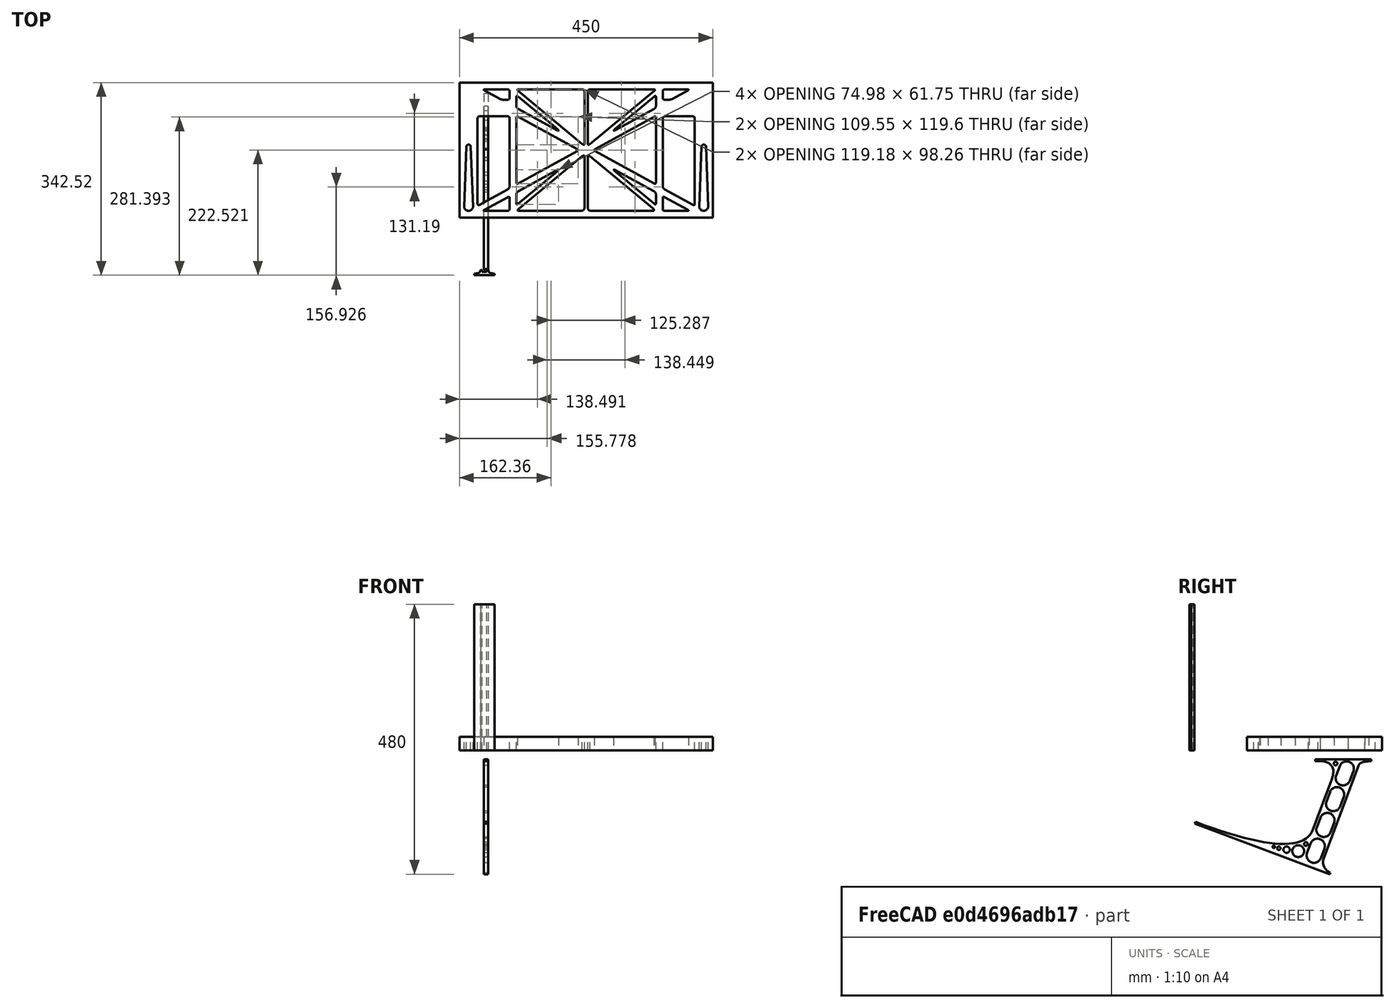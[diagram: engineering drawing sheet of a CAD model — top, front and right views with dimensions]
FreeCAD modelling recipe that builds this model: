
FCSTD DOCUMENT  (FreeCAD 0.19R0.19.2)
Label: laptopStand172FCStd
License: All rights reserved
LicenseURL: http://en.wikipedia.org/wiki/All_rights_reserved
objects: Sketcher::SketchObject×4, Part::Extrusion×3
note: 7 computed .brp shape members not serialized (recipe doc carries the construction recipe); baked Part::Feature solids carry a one-line shape summary decoded from their .brp

FEATURE [Sketcher::SketchObject] Sketch
  FullyConstrained = false
  sketch-geometry (349):
    g0: LineSegment StartX=-10.9272 StartY=-82.7794 StartZ=0 EndX=46.0728 EndY=-51.4823 EndZ=0
    g1: LineSegment StartX=-10.9272 StartY=76.4095 StartZ=0 EndX=-10.9272 EndY=-82.7794 EndZ=0
    g2: LineSegment StartX=46.0728 StartY=76.4095 StartZ=0 EndX=46.0728 EndY=-51.4823 EndZ=0
    g3: LineSegment StartX=-42.9272 StartY=136.221 StartZ=0 EndX=-42.9272 EndY=-103.779 EndZ=0
    g4: LineSegment StartX=407.073 StartY=136.221 StartZ=0 EndX=407.073 EndY=-103.779 EndZ=0
    g5: ArcOfCircle CenterX=-26.9272 CenterY=-83.7794 CenterZ=0 NormalX=0 NormalY=0 NormalZ=1 AngleXU=0 Radius=8 StartAngle=3.14159 EndAngle=6.28319
    g6: ArcOfCircle CenterX=391.073 CenterY=22.1087 CenterZ=0 NormalX=0 NormalY=0 NormalZ=1 AngleXU=0 Radius=8 StartAngle=-4.4e-15 EndAngle=3.14159
    g7: LineSegment StartX=399.073 StartY=22.1087 StartZ=0 EndX=399.073 EndY=-83.7794 EndZ=0
    g8: LineSegment StartX=383.073 StartY=22.1087 StartZ=0 EndX=383.073 EndY=-83.7794 EndZ=0
    g9: ArcOfCircle CenterX=391.073 CenterY=-83.7794 CenterZ=0 NormalX=0 NormalY=0 NormalZ=1 AngleXU=0 Radius=8 StartAngle=3.14159 EndAngle=6.28319
    g10: Circle CenterX=175.022 CenterY=27.0628 CenterZ=0 NormalX=0 NormalY=0 NormalZ=1 AngleXU=0 Radius=1
    g11: Circle CenterX=179.022 CenterY=24.8665 CenterZ=0 NormalX=0 NormalY=0 NormalZ=1 AngleXU=0 Radius=1
    g12: Circle CenterX=179.022 CenterY=27.0628 CenterZ=0 NormalX=0 NormalY=0 NormalZ=1 AngleXU=0 Radius=1
    g13: BSplineCurve PolesCount=3 KnotsCount=2 Degree=2 IsPeriodic=0
    g14: GeomPoint X=175.022 Y=27.0628 Z=0
    g15: GeomPoint X=179.022 Y=27.0628 Z=0
    g16: Circle CenterX=189.124 CenterY=27.0628 CenterZ=0 NormalX=0 NormalY=0 NormalZ=1 AngleXU=0 Radius=1
    g17: Circle CenterX=185.124 CenterY=24.8665 CenterZ=0 NormalX=0 NormalY=0 NormalZ=1 AngleXU=0 Radius=1
    g18: Circle CenterX=185.124 CenterY=27.0628 CenterZ=0 NormalX=0 NormalY=0 NormalZ=1 AngleXU=0 Radius=1
    g19: BSplineCurve PolesCount=3 KnotsCount=2 Degree=2 IsPeriodic=0
    g20: GeomPoint X=189.124 Y=27.0628 Z=0
    g21: GeomPoint X=185.124 Y=27.0628 Z=0
    g22: Circle CenterX=175.022 CenterY=5.37834 CenterZ=0 NormalX=0 NormalY=0 NormalZ=1 AngleXU=0 Radius=1
    g23: Circle CenterX=179.022 CenterY=7.57463 CenterZ=0 NormalX=0 NormalY=0 NormalZ=1 AngleXU=0 Radius=1
    g24: Circle CenterX=179.022 CenterY=5.34704 CenterZ=0 NormalX=0 NormalY=0 NormalZ=1 AngleXU=0 Radius=1
    g25: BSplineCurve PolesCount=3 KnotsCount=2 Degree=2 IsPeriodic=0
    g26: GeomPoint X=175.022 Y=5.37834 Z=0
    g27: GeomPoint X=179.022 Y=5.34704 Z=0
    g28: Circle CenterX=189.124 CenterY=5.37834 CenterZ=0 NormalX=0 NormalY=0 NormalZ=1 AngleXU=0 Radius=1
    g29: Circle CenterX=185.124 CenterY=7.57463 CenterZ=0 NormalX=0 NormalY=0 NormalZ=1 AngleXU=0 Radius=1
    g30: Circle CenterX=185.124 CenterY=5.34704 CenterZ=0 NormalX=0 NormalY=0 NormalZ=1 AngleXU=0 Radius=1
    g31: BSplineCurve PolesCount=3 KnotsCount=2 Degree=2 IsPeriodic=0
    g32: GeomPoint X=189.124 Y=5.37834 Z=0
    g33: GeomPoint X=185.124 Y=5.34704 Z=0
    g34: Circle CenterX=165.871 CenterY=18.1458 CenterZ=0 NormalX=0 NormalY=0 NormalZ=1 AngleXU=0 Radius=1
    g35: Circle CenterX=169.377 CenterY=16.2206 CenterZ=0 NormalX=0 NormalY=0 NormalZ=1 AngleXU=0 Radius=1
    g36: Circle CenterX=165.871 CenterY=14.2954 CenterZ=0 NormalX=0 NormalY=0 NormalZ=1 AngleXU=0 Radius=1
    g37: BSplineCurve PolesCount=3 KnotsCount=2 Degree=2 IsPeriodic=0
    g38: GeomPoint X=165.871 Y=18.1458 Z=0
    g39: GeomPoint X=165.871 Y=14.2954 Z=0
    g40: Circle CenterX=198.275 CenterY=18.1458 CenterZ=0 NormalX=0 NormalY=0 NormalZ=1 AngleXU=0 Radius=1
    g41: Circle CenterX=194.768 CenterY=16.2206 CenterZ=0 NormalX=0 NormalY=0 NormalZ=1 AngleXU=0 Radius=1
    g42: Circle CenterX=198.275 CenterY=14.2954 CenterZ=0 NormalX=0 NormalY=0 NormalZ=1 AngleXU=0 Radius=1
    g43: BSplineCurve PolesCount=3 KnotsCount=2 Degree=2 IsPeriodic=0
    g44: GeomPoint X=198.275 Y=18.1458 Z=0
    g45: GeomPoint X=198.275 Y=14.2954 Z=0
    g46: LineSegment StartX=407.073 StartY=-103.779 StartZ=0 EndX=-42.9272 EndY=-103.779 EndZ=0
    g47: LineSegment StartX=407.073 StartY=136.221 StartZ=0 EndX=-42.9272 EndY=136.221 EndZ=0
    g48: LineSegment StartX=46.0728 StartY=76.4095 StartZ=0 EndX=-10.9272 EndY=76.4095 EndZ=0
    g49: Circle CenterX=125.607 CenterY=54.1951 CenterZ=0 NormalX=0 NormalY=0 NormalZ=1 AngleXU=0 Radius=1
    g50: Circle CenterX=139.632 CenterY=46.4944 CenterZ=0 NormalX=0 NormalY=0 NormalZ=1 AngleXU=0 Radius=1
    g51: Circle CenterX=127.326 CenterY=56.7187 CenterZ=0 NormalX=0 NormalY=0 NormalZ=1 AngleXU=0 Radius=1
    g52: BSplineCurve PolesCount=3 KnotsCount=2 Degree=2 IsPeriodic=0
    g53: GeomPoint X=125.607 Y=54.1951 Z=0
    g54: GeomPoint X=127.326 Y=56.7187 Z=0
    g55: Circle CenterX=236.821 CenterY=56.7187 CenterZ=0 NormalX=0 NormalY=0 NormalZ=1 AngleXU=0 Radius=1
    g56: Circle CenterX=224.513 CenterY=46.4944 CenterZ=0 NormalX=0 NormalY=0 NormalZ=1 AngleXU=0 Radius=1
    g57: Circle CenterX=238.538 CenterY=54.1951 CenterZ=0 NormalX=0 NormalY=0 NormalZ=1 AngleXU=0 Radius=1
    g58: BSplineCurve PolesCount=3 KnotsCount=2 Degree=2 IsPeriodic=0
    g59: GeomPoint X=236.821 Y=56.7187 Z=0
    g60: GeomPoint X=238.538 Y=54.1951 Z=0
    g61: Circle CenterX=238.538 CenterY=-21.7539 CenterZ=0 NormalX=0 NormalY=0 NormalZ=1 AngleXU=0 Radius=1
    g62: Circle CenterX=224.513 CenterY=-14.0532 CenterZ=0 NormalX=0 NormalY=0 NormalZ=1 AngleXU=0 Radius=1
    g63: Circle CenterX=236.821 CenterY=-24.2775 CenterZ=0 NormalX=0 NormalY=0 NormalZ=1 AngleXU=0 Radius=1
    g64: BSplineCurve PolesCount=3 KnotsCount=2 Degree=2 IsPeriodic=0
    g65: GeomPoint X=238.538 Y=-21.7539 Z=0
    g66: GeomPoint X=236.821 Y=-24.2775 Z=0
    g67: Circle CenterX=125.607 CenterY=-21.7539 CenterZ=0 NormalX=0 NormalY=0 NormalZ=1 AngleXU=0 Radius=1
    g68: Circle CenterX=139.632 CenterY=-14.0532 CenterZ=0 NormalX=0 NormalY=0 NormalZ=1 AngleXU=0 Radius=1
    g69: Circle CenterX=127.325 CenterY=-24.2775 CenterZ=0 NormalX=0 NormalY=0 NormalZ=1 AngleXU=0 Radius=1
    g70: BSplineCurve PolesCount=3 KnotsCount=2 Degree=2 IsPeriodic=0
    g71: GeomPoint X=125.607 Y=-21.7539 Z=0
    g72: GeomPoint X=127.325 Y=-24.2775 Z=0
    g73: Circle CenterX=302.996 CenterY=111.695 CenterZ=0 NormalX=0 NormalY=0 NormalZ=1 AngleXU=0 Radius=1
    g74: Circle CenterX=306.073 CenterY=114.251 CenterZ=0 NormalX=0 NormalY=0 NormalZ=1 AngleXU=0 Radius=1
    g75: Circle CenterX=306.073 CenterY=110.251 CenterZ=0 NormalX=0 NormalY=0 NormalZ=1 AngleXU=0 Radius=1
    g76: BSplineCurve PolesCount=3 KnotsCount=2 Degree=2 IsPeriodic=0
    g77: GeomPoint X=302.996 Y=111.695 Z=0
    g78: GeomPoint X=306.073 Y=110.251 Z=0
    g79: Circle CenterX=306.073 CenterY=95.2763 CenterZ=0 NormalX=0 NormalY=0 NormalZ=1 AngleXU=0 Radius=1
    g80: Circle CenterX=306.073 CenterY=91.2763 CenterZ=0 NormalX=0 NormalY=0 NormalZ=1 AngleXU=0 Radius=1
    g81: Circle CenterX=302.567 CenterY=89.3511 CenterZ=0 NormalX=0 NormalY=0 NormalZ=1 AngleXU=0 Radius=1
    g82: BSplineCurve PolesCount=3 KnotsCount=2 Degree=2 IsPeriodic=0
    g83: GeomPoint X=306.073 Y=95.2763 Z=0
    g84: GeomPoint X=302.567 Y=89.3511 Z=0
    g85: LineSegment StartX=306.073 StartY=110.251 StartZ=0 EndX=306.073 EndY=95.2763 EndZ=0
    g86: LineSegment StartX=302.996 StartY=111.695 StartZ=0 EndX=236.821 EndY=56.7187 EndZ=0
    g87: LineSegment StartX=238.538 StartY=54.1951 StartZ=0 EndX=302.567 EndY=89.3511 EndZ=0
    g88: Circle CenterX=61.1496 CenterY=111.695 CenterZ=0 NormalX=0 NormalY=0 NormalZ=1 AngleXU=0 Radius=1
    g89: Circle CenterX=58.0728 CenterY=114.251 CenterZ=0 NormalX=0 NormalY=0 NormalZ=1 AngleXU=0 Radius=1
    g90: Circle CenterX=58.0728 CenterY=110.251 CenterZ=0 NormalX=0 NormalY=0 NormalZ=1 AngleXU=0 Radius=1
    g91: BSplineCurve PolesCount=3 KnotsCount=2 Degree=2 IsPeriodic=0
    g92: GeomPoint X=61.1496 Y=111.695 Z=0
    g93: GeomPoint X=58.0728 Y=110.251 Z=0
    g94: Circle CenterX=61.5791 CenterY=89.3511 CenterZ=0 NormalX=0 NormalY=0 NormalZ=1 AngleXU=0 Radius=1
    g95: Circle CenterX=58.0728 CenterY=91.2763 CenterZ=0 NormalX=0 NormalY=0 NormalZ=1 AngleXU=0 Radius=1
    g96: Circle CenterX=58.0728 CenterY=95.2763 CenterZ=0 NormalX=0 NormalY=0 NormalZ=1 AngleXU=0 Radius=1
    g97: BSplineCurve PolesCount=3 KnotsCount=2 Degree=2 IsPeriodic=0
    g98: GeomPoint X=61.5791 Y=89.3511 Z=0
    g99: GeomPoint X=58.0728 Y=95.2763 Z=0
    g100: LineSegment StartX=58.0728 StartY=110.251 StartZ=0 EndX=58.0728 EndY=95.2763 EndZ=0
    g101: LineSegment StartX=61.1496 StartY=111.695 StartZ=0 EndX=127.326 EndY=56.7187 EndZ=0
    g102: LineSegment StartX=125.607 StartY=54.1951 StartZ=0 EndX=61.5791 EndY=89.3511 EndZ=0
    g103: Circle CenterX=61.5791 CenterY=-56.9099 CenterZ=0 NormalX=0 NormalY=0 NormalZ=1 AngleXU=0 Radius=1
    g104: Circle CenterX=58.0728 CenterY=-58.8351 CenterZ=0 NormalX=0 NormalY=0 NormalZ=1 AngleXU=0 Radius=1
    g105: Circle CenterX=58.0728 CenterY=-62.8351 CenterZ=0 NormalX=0 NormalY=0 NormalZ=1 AngleXU=0 Radius=1
    g106: BSplineCurve PolesCount=3 KnotsCount=2 Degree=2 IsPeriodic=0
    g107: GeomPoint X=61.5791 Y=-56.9099 Z=0
    g108: GeomPoint X=58.0728 Y=-62.8351 Z=0
    g109: Circle CenterX=58.0728 CenterY=-77.8102 CenterZ=0 NormalX=0 NormalY=0 NormalZ=1 AngleXU=0 Radius=1
    g110: Circle CenterX=58.0728 CenterY=-81.8102 CenterZ=0 NormalX=0 NormalY=0 NormalZ=1 AngleXU=0 Radius=1
    g111: Circle CenterX=61.1496 CenterY=-79.2541 CenterZ=0 NormalX=0 NormalY=0 NormalZ=1 AngleXU=0 Radius=1
    g112: BSplineCurve PolesCount=3 KnotsCount=2 Degree=2 IsPeriodic=0
    g113: GeomPoint X=58.0728 Y=-77.8102 Z=0
    g114: GeomPoint X=61.1496 Y=-79.2541 Z=0
    g115: LineSegment StartX=58.0728 StartY=-62.8351 StartZ=0 EndX=58.0728 EndY=-77.8102 EndZ=0
    g116: LineSegment StartX=61.1496 StartY=-79.2541 StartZ=0 EndX=127.325 EndY=-24.2775 EndZ=0
    g117: LineSegment StartX=125.607 StartY=-21.7539 StartZ=0 EndX=61.5791 EndY=-56.9099 EndZ=0
    g118: Circle CenterX=302.567 CenterY=-56.9099 CenterZ=0 NormalX=0 NormalY=0 NormalZ=1 AngleXU=0 Radius=1
    g119: Circle CenterX=306.073 CenterY=-58.8351 CenterZ=0 NormalX=0 NormalY=0 NormalZ=1 AngleXU=0 Radius=1
    g120: Circle CenterX=306.073 CenterY=-62.8351 CenterZ=0 NormalX=0 NormalY=0 NormalZ=1 AngleXU=0 Radius=1
    g121: BSplineCurve PolesCount=3 KnotsCount=2 Degree=2 IsPeriodic=0
    g122: GeomPoint X=302.567 Y=-56.9099 Z=0
    g123: GeomPoint X=306.073 Y=-62.8351 Z=0
    g124: Circle CenterX=302.996 CenterY=-79.2541 CenterZ=0 NormalX=0 NormalY=0 NormalZ=1 AngleXU=0 Radius=1
    g125: Circle CenterX=306.073 CenterY=-81.8102 CenterZ=0 NormalX=0 NormalY=0 NormalZ=1 AngleXU=0 Radius=1
    g126: Circle CenterX=306.073 CenterY=-77.8102 CenterZ=0 NormalX=0 NormalY=0 NormalZ=1 AngleXU=0 Radius=1
    g127: BSplineCurve PolesCount=3 KnotsCount=2 Degree=2 IsPeriodic=0
    g128: GeomPoint X=302.996 Y=-79.2541 Z=0
    g129: GeomPoint X=306.073 Y=-77.8102 Z=0
    g130: LineSegment StartX=306.073 StartY=-62.8351 StartZ=0 EndX=306.073 EndY=-77.8102 EndZ=0
    g131: LineSegment StartX=302.996 StartY=-79.2541 StartZ=0 EndX=236.821 EndY=-24.2775 EndZ=0
    g132: LineSegment StartX=238.538 StartY=-21.7539 StartZ=0 EndX=302.567 EndY=-56.9099 EndZ=0
    g133: Circle CenterX=61.6457 CenterY=-88.8112 CenterZ=0 NormalX=0 NormalY=0 NormalZ=1 AngleXU=0 Radius=1
    g134: Circle CenterX=58.0728 CenterY=-91.7794 CenterZ=0 NormalX=0 NormalY=0 NormalZ=1 AngleXU=0 Radius=1
    g135: Circle CenterX=63.9135 CenterY=-91.7794 CenterZ=0 NormalX=0 NormalY=0 NormalZ=1 AngleXU=0 Radius=1
    g136: BSplineCurve PolesCount=3 KnotsCount=2 Degree=2 IsPeriodic=0
    g137: GeomPoint X=61.6457 Y=-88.8112 Z=0
    g138: GeomPoint X=63.9135 Y=-91.7794 Z=0
    g139: Circle CenterX=179.022 CenterY=-85.8163 CenterZ=0 NormalX=0 NormalY=0 NormalZ=1 AngleXU=0 Radius=1
    g140: Circle CenterX=179.022 CenterY=-91.7794 CenterZ=0 NormalX=0 NormalY=0 NormalZ=1 AngleXU=0 Radius=1
    g141: Circle CenterX=171.895 CenterY=-91.7794 CenterZ=0 NormalX=0 NormalY=0 NormalZ=1 AngleXU=0 Radius=1
    g142: BSplineCurve PolesCount=3 KnotsCount=2 Degree=2 IsPeriodic=0
    g143: GeomPoint X=179.022 Y=-85.8163 Z=0
    g144: GeomPoint X=171.895 Y=-91.7794 Z=0
    g145: Circle CenterX=185.124 CenterY=-86.2028 CenterZ=0 NormalX=0 NormalY=0 NormalZ=1 AngleXU=0 Radius=1
    g146: Circle CenterX=185.124 CenterY=-91.7794 CenterZ=0 NormalX=0 NormalY=0 NormalZ=1 AngleXU=0 Radius=1
    g147: Circle CenterX=191.747 CenterY=-91.7794 CenterZ=0 NormalX=0 NormalY=0 NormalZ=1 AngleXU=0 Radius=1
    g148: BSplineCurve PolesCount=3 KnotsCount=2 Degree=2 IsPeriodic=0
    g149: GeomPoint X=185.124 Y=-86.2028 Z=0
    g150: GeomPoint X=191.747 Y=-91.7794 Z=0
    g151: Circle CenterX=299.888 CenterY=-86.6413 CenterZ=0 NormalX=0 NormalY=0 NormalZ=1 AngleXU=0 Radius=1
    g152: Circle CenterX=306.073 CenterY=-91.7794 CenterZ=0 NormalX=0 NormalY=0 NormalZ=1 AngleXU=0 Radius=1
    g153: Circle CenterX=298.776 CenterY=-91.7794 CenterZ=0 NormalX=0 NormalY=0 NormalZ=1 AngleXU=0 Radius=1
    g154: BSplineCurve PolesCount=3 KnotsCount=2 Degree=2 IsPeriodic=0
    g155: GeomPoint X=299.888 Y=-86.6413 Z=0
    g156: GeomPoint X=298.776 Y=-91.7794 Z=0
    g157: LineSegment StartX=189.124 StartY=5.37834 StartZ=0 EndX=299.888 EndY=-86.6413 EndZ=0
    g158: LineSegment StartX=298.776 StartY=-91.7794 StartZ=0 EndX=191.747 EndY=-91.7794 EndZ=0
    g159: LineSegment StartX=185.124 StartY=-86.2028 StartZ=0 EndX=185.124 EndY=5.34704 EndZ=0
    g160: LineSegment StartX=179.022 StartY=5.34704 StartZ=0 EndX=179.022 EndY=-85.8163 EndZ=0
    g161: LineSegment StartX=171.895 StartY=-91.7794 StartZ=0 EndX=63.9135 EndY=-91.7794 EndZ=0
    g162: LineSegment StartX=61.6457 StartY=-88.8112 StartZ=0 EndX=175.022 EndY=5.37834 EndZ=0
    g163: Circle CenterX=302.073 CenterY=124.221 CenterZ=0 NormalX=0 NormalY=0 NormalZ=1 AngleXU=0 Radius=1
    g164: Circle CenterX=306.073 CenterY=124.221 CenterZ=0 NormalX=0 NormalY=0 NormalZ=1 AngleXU=0 Radius=1
    g165: Circle CenterX=302.996 CenterY=121.665 CenterZ=0 NormalX=0 NormalY=0 NormalZ=1 AngleXU=0 Radius=1
    g166: BSplineCurve PolesCount=3 KnotsCount=2 Degree=2 IsPeriodic=0
    g167: GeomPoint X=302.073 Y=124.221 Z=0
    g168: GeomPoint X=302.996 Y=121.665 Z=0
    g169: Circle CenterX=189.124 CenterY=124.221 CenterZ=0 NormalX=0 NormalY=0 NormalZ=1 AngleXU=0 Radius=1
    g170: Circle CenterX=185.124 CenterY=124.221 CenterZ=0 NormalX=0 NormalY=0 NormalZ=1 AngleXU=0 Radius=1
    g171: Circle CenterX=185.124 CenterY=120.221 CenterZ=0 NormalX=0 NormalY=0 NormalZ=1 AngleXU=0 Radius=1
    g172: BSplineCurve PolesCount=3 KnotsCount=2 Degree=2 IsPeriodic=0
    g173: GeomPoint X=189.124 Y=124.221 Z=0
    g174: GeomPoint X=185.124 Y=120.221 Z=0
    g175: Circle CenterX=175.022 CenterY=124.221 CenterZ=0 NormalX=0 NormalY=0 NormalZ=1 AngleXU=0 Radius=1
    g176: Circle CenterX=179.022 CenterY=124.221 CenterZ=0 NormalX=0 NormalY=0 NormalZ=1 AngleXU=0 Radius=1
    g177: Circle CenterX=179.022 CenterY=120.221 CenterZ=0 NormalX=0 NormalY=0 NormalZ=1 AngleXU=0 Radius=1
    g178: BSplineCurve PolesCount=3 KnotsCount=2 Degree=2 IsPeriodic=0
    g179: GeomPoint X=175.022 Y=124.221 Z=0
    g180: GeomPoint X=179.022 Y=120.221 Z=0
    g181: Circle CenterX=62.0728 CenterY=124.221 CenterZ=0 NormalX=0 NormalY=0 NormalZ=1 AngleXU=0 Radius=1
    g182: Circle CenterX=58.0728 CenterY=124.221 CenterZ=0 NormalX=0 NormalY=0 NormalZ=1 AngleXU=0 Radius=1
    g183: Circle CenterX=61.1496 CenterY=121.665 CenterZ=0 NormalX=0 NormalY=0 NormalZ=1 AngleXU=0 Radius=1
    g184: BSplineCurve PolesCount=3 KnotsCount=2 Degree=2 IsPeriodic=0
    g185: GeomPoint X=62.0728 Y=124.221 Z=0
    g186: GeomPoint X=61.1496 Y=121.665 Z=0
    g187: LineSegment StartX=62.0728 StartY=124.221 StartZ=0 EndX=175.022 EndY=124.221 EndZ=0
    g188: LineSegment StartX=179.022 StartY=120.221 StartZ=0 EndX=179.022 EndY=27.0628 EndZ=0
    g189: LineSegment StartX=185.124 StartY=27.0628 StartZ=0 EndX=185.124 EndY=120.221 EndZ=0
    g190: LineSegment StartX=189.124 StartY=124.221 StartZ=0 EndX=302.073 EndY=124.221 EndZ=0
    g191: LineSegment StartX=302.996 StartY=121.665 StartZ=0 EndX=189.124 EndY=27.0628 EndZ=0
    g192: LineSegment StartX=175.022 StartY=27.0628 StartZ=0 EndX=61.1496 EndY=121.665 EndZ=0
    g193: Circle CenterX=61.5791 CenterY=75.4095 CenterZ=0 NormalX=0 NormalY=0 NormalZ=1 AngleXU=0 Radius=1
    g194: Circle CenterX=58.0728 CenterY=77.3346 CenterZ=0 NormalX=0 NormalY=0 NormalZ=1 AngleXU=0 Radius=1
    g195: Circle CenterX=58.0728 CenterY=73.3346 CenterZ=0 NormalX=0 NormalY=0 NormalZ=1 AngleXU=0 Radius=1
    g196: BSplineCurve PolesCount=3 KnotsCount=2 Degree=2 IsPeriodic=0
    g197: GeomPoint X=61.5791 Y=75.4095 Z=0
    g198: GeomPoint X=58.0728 Y=73.3346 Z=0
    g199: Circle CenterX=58.0728 CenterY=-40.8935 CenterZ=0 NormalX=0 NormalY=0 NormalZ=1 AngleXU=0 Radius=1
    g200: Circle CenterX=58.0728 CenterY=-44.8935 CenterZ=0 NormalX=0 NormalY=0 NormalZ=1 AngleXU=0 Radius=1
    g201: Circle CenterX=61.5791 CenterY=-42.9683 CenterZ=0 NormalX=0 NormalY=0 NormalZ=1 AngleXU=0 Radius=1
    g202: BSplineCurve PolesCount=3 KnotsCount=2 Degree=2 IsPeriodic=0
    g203: GeomPoint X=58.0728 Y=-40.8935 Z=0
    g204: GeomPoint X=61.5791 Y=-42.9683 Z=0
    g205: LineSegment StartX=61.5791 StartY=-42.9683 StartZ=0 EndX=165.871 EndY=14.2954 EndZ=0
    g206: LineSegment StartX=165.871 StartY=18.1458 StartZ=0 EndX=61.5791 EndY=75.4095 EndZ=0
    g207: LineSegment StartX=58.0728 StartY=73.3346 StartZ=0 EndX=58.0728 EndY=-40.8935 EndZ=0
    g208: Circle CenterX=302.567 CenterY=-42.9683 CenterZ=0 NormalX=0 NormalY=0 NormalZ=1 AngleXU=0 Radius=1
    g209: Circle CenterX=306.073 CenterY=-44.8935 CenterZ=0 NormalX=0 NormalY=0 NormalZ=1 AngleXU=0 Radius=1
    g210: Circle CenterX=306.073 CenterY=-40.8935 CenterZ=0 NormalX=0 NormalY=0 NormalZ=1 AngleXU=0 Radius=1
    g211: BSplineCurve PolesCount=3 KnotsCount=2 Degree=2 IsPeriodic=0
    g212: GeomPoint X=302.567 Y=-42.9683 Z=0
    g213: GeomPoint X=306.073 Y=-40.8935 Z=0
    g214: Circle CenterX=306.073 CenterY=73.3346 CenterZ=0 NormalX=0 NormalY=0 NormalZ=1 AngleXU=0 Radius=1
    g215: Circle CenterX=306.073 CenterY=77.3346 CenterZ=0 NormalX=0 NormalY=0 NormalZ=1 AngleXU=0 Radius=1
    g216: Circle CenterX=302.567 CenterY=75.4095 CenterZ=0 NormalX=0 NormalY=0 NormalZ=1 AngleXU=0 Radius=1
    g217: BSplineCurve PolesCount=3 KnotsCount=2 Degree=2 IsPeriodic=0
    g218: GeomPoint X=306.073 Y=73.3346 Z=0
    g219: GeomPoint X=302.567 Y=75.4095 Z=0
    g220: LineSegment StartX=302.567 StartY=-42.9683 StartZ=0 EndX=198.275 EndY=14.2954 EndZ=0
    g221: LineSegment StartX=198.275 StartY=18.1458 StartZ=0 EndX=302.567 EndY=75.4095 EndZ=0
    g222: LineSegment StartX=306.073 StartY=73.3346 StartZ=0 EndX=306.073 EndY=-40.8935 EndZ=0
    g223: LineSegment StartX=322.073 StartY=105.865 StartZ=0 EndX=328.643 EndY=105.865 EndZ=0
    g224: LineSegment StartX=318.073 StartY=120.221 StartZ=0 EndX=318.073 EndY=109.865 EndZ=0
    g225: LineSegment StartX=336.157 StartY=107.779 StartZ=0 EndX=362.567 EndY=122.294 EndZ=0
    g226: Circle CenterX=362.073 CenterY=124.221 CenterZ=0 NormalX=0 NormalY=0 NormalZ=1 AngleXU=0 Radius=1
    g227: Circle CenterX=366.073 CenterY=124.221 CenterZ=0 NormalX=0 NormalY=0 NormalZ=1 AngleXU=0 Radius=1
    g228: Circle CenterX=362.567 CenterY=122.294 CenterZ=0 NormalX=0 NormalY=0 NormalZ=1 AngleXU=0 Radius=1
    g229: BSplineCurve PolesCount=3 KnotsCount=2 Degree=2 IsPeriodic=0
    g230: GeomPoint X=362.073 Y=124.221 Z=0
    g231: GeomPoint X=362.567 Y=122.294 Z=0
    g232: Circle CenterX=322.073 CenterY=124.221 CenterZ=0 NormalX=0 NormalY=0 NormalZ=1 AngleXU=0 Radius=1
    g233: Circle CenterX=318.073 CenterY=124.221 CenterZ=0 NormalX=0 NormalY=0 NormalZ=1 AngleXU=0 Radius=1
    g234: Circle CenterX=318.073 CenterY=120.221 CenterZ=0 NormalX=0 NormalY=0 NormalZ=1 AngleXU=0 Radius=1
    g235: BSplineCurve PolesCount=3 KnotsCount=2 Degree=2 IsPeriodic=0
    g236: GeomPoint X=322.073 Y=124.221 Z=0
    g237: GeomPoint X=318.073 Y=120.221 Z=0
    g238: Circle CenterX=322.073 CenterY=105.865 CenterZ=0 NormalX=0 NormalY=0 NormalZ=1 AngleXU=0 Radius=1
    g239: Circle CenterX=318.073 CenterY=105.865 CenterZ=0 NormalX=0 NormalY=0 NormalZ=1 AngleXU=0 Radius=1
    g240: Circle CenterX=318.073 CenterY=109.865 CenterZ=0 NormalX=0 NormalY=0 NormalZ=1 AngleXU=0 Radius=1
    g241: BSplineCurve PolesCount=3 KnotsCount=2 Degree=2 IsPeriodic=0
    g242: GeomPoint X=322.073 Y=105.865 Z=0
    g243: GeomPoint X=318.073 Y=109.865 Z=0
    g244: Circle CenterX=336.157 CenterY=107.779 CenterZ=0 NormalX=0 NormalY=0 NormalZ=1 AngleXU=0 Radius=1
    g245: Circle CenterX=332.651 CenterY=105.853 CenterZ=0 NormalX=0 NormalY=0 NormalZ=1 AngleXU=0 Radius=1
    g246: Circle CenterX=328.643 CenterY=105.865 CenterZ=0 NormalX=0 NormalY=0 NormalZ=1 AngleXU=0 Radius=1
    g247: BSplineCurve PolesCount=3 KnotsCount=2 Degree=2 IsPeriodic=0
    g248: GeomPoint X=336.157 Y=107.779 Z=0
    g249: GeomPoint X=328.643 Y=105.865 Z=0
    g250: LineSegment StartX=322.073 StartY=124.221 StartZ=0 EndX=362.073 EndY=124.221 EndZ=0
    g251: Circle CenterX=371.567 CenterY=-80.8644 CenterZ=0 NormalX=0 NormalY=0 NormalZ=1 AngleXU=0 Radius=1
    g252: Circle CenterX=375.073 CenterY=-82.7896 CenterZ=0 NormalX=0 NormalY=0 NormalZ=1 AngleXU=0 Radius=1
    g253: Circle CenterX=375.073 CenterY=-78.7896 CenterZ=0 NormalX=0 NormalY=0 NormalZ=1 AngleXU=0 Radius=1
    g254: BSplineCurve PolesCount=3 KnotsCount=2 Degree=2 IsPeriodic=0
    g255: GeomPoint X=371.567 Y=-80.8644 Z=0
    g256: GeomPoint X=375.073 Y=-78.7896 Z=0
    g257: Circle CenterX=321.579 CenterY=-53.4075 CenterZ=0 NormalX=0 NormalY=0 NormalZ=1 AngleXU=0 Radius=1
    g258: Circle CenterX=318.073 CenterY=-51.4823 CenterZ=0 NormalX=0 NormalY=0 NormalZ=1 AngleXU=0 Radius=1
    g259: Circle CenterX=318.073 CenterY=-47.4805 CenterZ=0 NormalX=0 NormalY=0 NormalZ=1 AngleXU=0 Radius=1
    g260: BSplineCurve PolesCount=3 KnotsCount=2 Degree=2 IsPeriodic=0
    g261: GeomPoint X=321.579 Y=-53.4075 Z=0
    g262: GeomPoint X=318.073 Y=-47.4805 Z=0
    g263: LineSegment StartX=371.567 StartY=-80.8644 StartZ=0 EndX=321.579 EndY=-53.4075 EndZ=0
    g264: Circle CenterX=321.579 CenterY=-67.3492 CenterZ=0 NormalX=0 NormalY=0 NormalZ=1 AngleXU=0 Radius=1
    g265: Circle CenterX=318.073 CenterY=-65.424 CenterZ=0 NormalX=0 NormalY=0 NormalZ=1 AngleXU=0 Radius=1
    g266: Circle CenterX=318.073 CenterY=-69.424 CenterZ=0 NormalX=0 NormalY=0 NormalZ=1 AngleXU=0 Radius=1
    g267: BSplineCurve PolesCount=3 KnotsCount=2 Degree=2 IsPeriodic=0
    g268: GeomPoint X=321.579 Y=-67.3492 Z=0
    g269: GeomPoint X=318.073 Y=-69.424 Z=0
    g270: Circle CenterX=362.567 CenterY=-89.8542 CenterZ=0 NormalX=0 NormalY=0 NormalZ=1 AngleXU=0 Radius=1
    g271: Circle CenterX=366.073 CenterY=-91.7794 CenterZ=0 NormalX=0 NormalY=0 NormalZ=1 AngleXU=0 Radius=1
    g272: Circle CenterX=362.073 CenterY=-91.7794 CenterZ=0 NormalX=0 NormalY=0 NormalZ=1 AngleXU=0 Radius=1
    g273: BSplineCurve PolesCount=3 KnotsCount=2 Degree=2 IsPeriodic=0
    g274: GeomPoint X=362.567 Y=-89.8542 Z=0
    g275: GeomPoint X=362.073 Y=-91.7794 Z=0
    g276: Circle CenterX=322.073 CenterY=-91.7794 CenterZ=0 NormalX=0 NormalY=0 NormalZ=1 AngleXU=0 Radius=1
    g277: Circle CenterX=318.073 CenterY=-91.7794 CenterZ=0 NormalX=0 NormalY=0 NormalZ=1 AngleXU=0 Radius=1
    g278: Circle CenterX=318.073 CenterY=-87.7794 CenterZ=0 NormalX=0 NormalY=0 NormalZ=1 AngleXU=0 Radius=1
    g279: BSplineCurve PolesCount=3 KnotsCount=2 Degree=2 IsPeriodic=0
    g280: GeomPoint X=322.073 Y=-91.7794 Z=0
    g281: GeomPoint X=318.073 Y=-87.7794 Z=0
    g282: LineSegment StartX=362.567 StartY=-89.8542 StartZ=0 EndX=321.579 EndY=-67.3492 EndZ=0
    g283: LineSegment StartX=318.073 StartY=-69.424 StartZ=0 EndX=318.073 EndY=-87.7794 EndZ=0
    g284: LineSegment StartX=322.073 StartY=-91.7794 StartZ=0 EndX=362.073 EndY=-91.7794 EndZ=0
    g285: Circle CenterX=2.07281 CenterY=124.221 CenterZ=0 NormalX=0 NormalY=0 NormalZ=1 AngleXU=0 Radius=1
    g286: Circle CenterX=1.57905 CenterY=122.295 CenterZ=0 NormalX=0 NormalY=0 NormalZ=1 AngleXU=0 Radius=1
    g287: BSplineCurve PolesCount=3 KnotsCount=2 Degree=2 IsPeriodic=0
    g288: GeomPoint X=2.07281 Y=124.221 Z=0
    g289: GeomPoint X=1.57905 Y=122.295 Z=0
    g290: Circle CenterX=42.0728 CenterY=124.221 CenterZ=0 NormalX=0 NormalY=0 NormalZ=1 AngleXU=0 Radius=1
    g291: Circle CenterX=46.0728 CenterY=124.221 CenterZ=0 NormalX=0 NormalY=0 NormalZ=1 AngleXU=0 Radius=1
    g292: Circle CenterX=46.0728 CenterY=120.221 CenterZ=0 NormalX=0 NormalY=0 NormalZ=1 AngleXU=0 Radius=1
    g293: BSplineCurve PolesCount=3 KnotsCount=2 Degree=2 IsPeriodic=0
    g294: GeomPoint X=42.0728 Y=124.221 Z=0
    g295: GeomPoint X=46.0728 Y=120.221 Z=0
    g296: Circle CenterX=46.0728 CenterY=109.865 CenterZ=0 NormalX=0 NormalY=0 NormalZ=1 AngleXU=0 Radius=1
    g297: Circle CenterX=46.0728 CenterY=105.865 CenterZ=0 NormalX=0 NormalY=0 NormalZ=1 AngleXU=0 Radius=1
    g298: Circle CenterX=42.0728 CenterY=105.865 CenterZ=0 NormalX=0 NormalY=0 NormalZ=1 AngleXU=0 Radius=1
    g299: BSplineCurve PolesCount=3 KnotsCount=2 Degree=2 IsPeriodic=0
    g300: GeomPoint X=46.0728 Y=109.865 Z=0
    g301: GeomPoint X=42.0728 Y=105.865 Z=0
    g302: Circle CenterX=35.5028 CenterY=105.865 CenterZ=0 NormalX=0 NormalY=0 NormalZ=1 AngleXU=0 Radius=1
    g303: Circle CenterX=31.5028 CenterY=105.865 CenterZ=0 NormalX=0 NormalY=0 NormalZ=1 AngleXU=0 Radius=1
    g304: Circle CenterX=27.9965 CenterY=107.79 CenterZ=0 NormalX=0 NormalY=0 NormalZ=1 AngleXU=0 Radius=1
    g305: BSplineCurve PolesCount=3 KnotsCount=2 Degree=2 IsPeriodic=0
    g306: GeomPoint X=35.5028 Y=105.865 Z=0
    g307: GeomPoint X=27.9965 Y=107.79 Z=0
    g308: LineSegment StartX=2.07281 StartY=124.221 StartZ=0 EndX=42.0728 EndY=124.221 EndZ=0
    g309: LineSegment StartX=46.0728 StartY=120.221 StartZ=0 EndX=46.0728 EndY=109.865 EndZ=0
    g310: LineSegment StartX=42.0728 StartY=105.865 StartZ=0 EndX=35.5028 EndY=105.865 EndZ=0
    g311: LineSegment StartX=27.9965 StartY=107.79 StartZ=0 EndX=1.57905 EndY=122.295 EndZ=0
    g312: Circle CenterX=42.5666 CenterY=-67.3492 CenterZ=0 NormalX=0 NormalY=0 NormalZ=1 AngleXU=0 Radius=1
    g313: Circle CenterX=46.0728 CenterY=-65.424 CenterZ=0 NormalX=0 NormalY=0 NormalZ=1 AngleXU=0 Radius=1
    g314: Circle CenterX=46.0728 CenterY=-69.424 CenterZ=0 NormalX=0 NormalY=0 NormalZ=1 AngleXU=0 Radius=1
    g315: BSplineCurve PolesCount=3 KnotsCount=2 Degree=2 IsPeriodic=0
    g316: GeomPoint X=42.5666 Y=-67.3492 Z=0
    g317: GeomPoint X=46.0728 Y=-69.424 Z=0
    g318: Circle CenterX=46.0728 CenterY=-87.7794 CenterZ=0 NormalX=0 NormalY=0 NormalZ=1 AngleXU=0 Radius=1
    g319: Circle CenterX=46.0728 CenterY=-91.7794 CenterZ=0 NormalX=0 NormalY=0 NormalZ=1 AngleXU=0 Radius=1
    g320: Circle CenterX=42.0728 CenterY=-91.7794 CenterZ=0 NormalX=0 NormalY=0 NormalZ=1 AngleXU=0 Radius=1
    g321: BSplineCurve PolesCount=3 KnotsCount=2 Degree=2 IsPeriodic=0
    g322: GeomPoint X=46.0728 Y=-87.7794 Z=0
    g323: GeomPoint X=42.0728 Y=-91.7794 Z=0
    g324: Circle CenterX=2.07281 CenterY=-91.7794 CenterZ=0 NormalX=0 NormalY=0 NormalZ=1 AngleXU=0 Radius=1
    g325: Circle CenterX=-1.92719 CenterY=-91.7794 CenterZ=0 NormalX=0 NormalY=0 NormalZ=1 AngleXU=0 Radius=1
    g326: Circle CenterX=1.57905 CenterY=-89.8542 CenterZ=0 NormalX=0 NormalY=0 NormalZ=1 AngleXU=0 Radius=1
    g327: BSplineCurve PolesCount=3 KnotsCount=2 Degree=2 IsPeriodic=0
    g328: GeomPoint X=2.07281 Y=-91.7794 Z=0
    g329: GeomPoint X=1.57905 Y=-89.8542 Z=0
    g330: LineSegment StartX=2.07281 StartY=-91.7794 StartZ=0 EndX=42.0728 EndY=-91.7794 EndZ=0
    g331: LineSegment StartX=46.0728 StartY=-87.7794 StartZ=0 EndX=46.0728 EndY=-69.424 EndZ=0
    g332: LineSegment StartX=42.5666 StartY=-67.3492 StartZ=0 EndX=1.57905 EndY=-89.8542 EndZ=0
    g333: Circle CenterX=322.073 CenterY=76.4095 CenterZ=0 NormalX=0 NormalY=0 NormalZ=1 AngleXU=0 Radius=4
    g334: BSplineCurve PolesCount=3 KnotsCount=2 Degree=2 IsPeriodic=0
    g335: GeomPoint X=318.073 Y=72.4095 Z=0
    g336: GeomPoint X=322.073 Y=76.4095 Z=0
    g337: Circle CenterX=375.073 CenterY=72.4095 CenterZ=0 NormalX=0 NormalY=0 NormalZ=1 AngleXU=0 Radius=1
    g338: Circle CenterX=375.073 CenterY=76.4095 CenterZ=0 NormalX=0 NormalY=0 NormalZ=1 AngleXU=0 Radius=1
    g339: Circle CenterX=371.073 CenterY=76.4095 CenterZ=0 NormalX=0 NormalY=0 NormalZ=1 AngleXU=0 Radius=1
    g340: BSplineCurve PolesCount=3 KnotsCount=2 Degree=2 IsPeriodic=0
    g341: GeomPoint X=375.073 Y=72.4095 Z=0
    g342: GeomPoint X=371.073 Y=76.4095 Z=0
    g343: LineSegment StartX=322.073 StartY=76.4095 StartZ=0 EndX=371.073 EndY=76.4095 EndZ=0
    g344: LineSegment StartX=318.073 StartY=72.4095 StartZ=0 EndX=318.073 EndY=-47.4805 EndZ=0
    g345: LineSegment StartX=375.073 StartY=72.4095 StartZ=0 EndX=375.073 EndY=-78.7896 EndZ=0
    g346: ArcOfCircle CenterX=-26.9272 CenterY=22.1087 CenterZ=0 NormalX=0 NormalY=0 NormalZ=1 AngleXU=0 Radius=4 StartAngle=5e-16 EndAngle=3.14159
    g347: LineSegment StartX=-30.9272 StartY=22.1087 StartZ=0 EndX=-34.9272 EndY=-83.7794 EndZ=0
    g348: LineSegment StartX=-18.9272 StartY=-83.7794 StartZ=0 EndX=-22.9272 EndY=22.1087 EndZ=0
  constraints (572):
    c: Coincident(g0,g2)
    c: Block(g0)
    c: Block(g1)
    c: Vertical(g3)
    c: Vertical(g4)
    c: Block(g4)
    c: Block(g3)
    c: Tangent(g6,g7) = 1.5708
    c: Tangent(g7,g9) = 1.5708
    c: Equal(g6,g9)
    c: Coincident(g8,g6)
    c: Coincident(g8,g9)
    c: Block(g7)
    c: Block(g8)
    c: Weight(g10) = 1
    c: Equal(g10,g11)
    c: Equal(g10,g12)
    c: InternalAlignment(g10,g13)
    c: InternalAlignment(g11,g13)
    c: InternalAlignment(g12,g13)
    c: InternalAlignment(g14,g13)
    c: InternalAlignment(g15,g13)
    c: Weight(g16) = 1
    c: Equal(g16,g17)
    c: Equal(g16,g18)
    c: InternalAlignment(g16,g19)
    c: InternalAlignment(g17,g19)
    c: InternalAlignment(g18,g19)
    c: InternalAlignment(g20,g19)
    c: InternalAlignment(g21,g19)
    c: Block(g19)
    c: Block(g13)
    c: Weight(g22) = 1
    c: Equal(g22,g23)
    c: Equal(g22,g24)
    c: InternalAlignment(g22,g25)
    c: InternalAlignment(g23,g25)
    c: InternalAlignment(g24,g25)
    c: InternalAlignment(g26,g25)
    c: InternalAlignment(g27,g25)
    c: Weight(g28) = 1
    c: Equal(g28,g29)
    c: Equal(g28,g30)
    c: InternalAlignment(g28,g31)
    c: InternalAlignment(g29,g31)
    c: InternalAlignment(g30,g31)
    c: InternalAlignment(g32,g31)
    c: InternalAlignment(g33,g31)
    c: Block(g31)
    c: Block(g25)
    c: Weight(g34) = 1
    c: Equal(g34,g35)
    c: Equal(g34,g36)
    c: InternalAlignment(g34,g37)
    c: InternalAlignment(g35,g37)
    c: InternalAlignment(g36,g37)
    c: InternalAlignment(g38,g37)
    c: InternalAlignment(g39,g37)
    c: Weight(g40) = 1
    c: Equal(g40,g41)
    c: Equal(g40,g42)
    c: InternalAlignment(g40,g43)
    c: InternalAlignment(g41,g43)
    c: InternalAlignment(g42,g43)
    c: InternalAlignment(g44,g43)
    c: InternalAlignment(g45,g43)
    c: Block(g37)
    c: Block(g43)
    c: Coincident(g46,g4)
    c: Coincident(g46,g3)
    c: Horizontal(g46)
    c: Distance(g46) = 450
    c: Coincident(g47,g4)
    c: Coincident(g47,g3)
    c: Horizontal(g47)
    c: Horizontal(g48)
    c: Coincident(g2,g48)
    c: Block(g48)
    c: Coincident(g1,g48)
    c: Weight(g49) = 1
    c: Equal(g49,g50)
    c: Equal(g49,g51)
    c: InternalAlignment(g49,g52)
    c: InternalAlignment(g50,g52)
    c: InternalAlignment(g51,g52)
    c: InternalAlignment(g53,g52)
    c: InternalAlignment(g54,g52)
    c: Block(g52)
    c: Weight(g55) = 1
    c: Equal(g55,g56)
    c: Equal(g55,g57)
    c: InternalAlignment(g55,g58)
    c: InternalAlignment(g56,g58)
    c: InternalAlignment(g57,g58)
    c: InternalAlignment(g59,g58)
    c: InternalAlignment(g60,g58)
    c: Block(g58)
    c: Weight(g61) = 1
    c: Equal(g61,g62)
    c: Equal(g61,g63)
    c: InternalAlignment(g61,g64)
    c: InternalAlignment(g62,g64)
    c: InternalAlignment(g63,g64)
    c: InternalAlignment(g65,g64)
    c: InternalAlignment(g66,g64)
    c: Block(g64)
    c: Weight(g67) = 1
    c: Equal(g67,g68)
    c: Equal(g67,g69)
    c: InternalAlignment(g67,g70)
    c: InternalAlignment(g68,g70)
    c: InternalAlignment(g69,g70)
    c: InternalAlignment(g71,g70)
    c: InternalAlignment(g72,g70)
    c: Block(g70)
    c: Weight(g73) = 1
    c: Equal(g73,g74)
    c: Equal(g73,g75)
    c: InternalAlignment(g73,g76)
    c: InternalAlignment(g74,g76)
    c: InternalAlignment(g75,g76)
    c: InternalAlignment(g77,g76)
    c: InternalAlignment(g78,g76)
    c: Weight(g79) = 1
    c: Equal(g79,g80)
    c: Equal(g79,g81)
    c: InternalAlignment(g79,g82)
    c: InternalAlignment(g80,g82)
    c: InternalAlignment(g81,g82)
    c: InternalAlignment(g83,g82)
    c: InternalAlignment(g84,g82)
    c: Block(g76)
    c: Block(g82)
    c: Coincident(g85,g76)
    c: Coincident(g85,g82)
    c: Vertical(g85)
    c: Coincident(g86,g76)
    c: Coincident(g86,g58)
    c: Coincident(g87,g58)
    c: Coincident(g87,g82)
    c: Weight(g88) = 1
    c: Equal(g88,g89)
    c: Equal(g88,g90)
    c: InternalAlignment(g88,g91)
    c: InternalAlignment(g89,g91)
    c: InternalAlignment(g90,g91)
    c: InternalAlignment(g92,g91)
    c: InternalAlignment(g93,g91)
    c: Weight(g94) = 1
    c: Equal(g94,g95)
    c: Equal(g94,g96)
    c: InternalAlignment(g94,g97)
    c: InternalAlignment(g95,g97)
    c: InternalAlignment(g96,g97)
    c: InternalAlignment(g98,g97)
    c: InternalAlignment(g99,g97)
    c: Block(g91)
    c: Block(g97)
    c: Coincident(g100,g91)
    c: Coincident(g100,g97)
    c: Vertical(g100)
    c: Coincident(g101,g91)
    c: Coincident(g101,g52)
    c: Coincident(g102,g52)
    c: Coincident(g102,g97)
    c: Weight(g103) = 1
    c: Equal(g103,g104)
    c: Equal(g103,g105)
    c: InternalAlignment(g103,g106)
    c: InternalAlignment(g104,g106)
    c: InternalAlignment(g105,g106)
    c: InternalAlignment(g107,g106)
    c: InternalAlignment(g108,g106)
    c: Weight(g109) = 1
    c: Equal(g109,g110)
    c: Equal(g109,g111)
    c: InternalAlignment(g109,g112)
    c: InternalAlignment(g110,g112)
    c: InternalAlignment(g111,g112)
    c: InternalAlignment(g113,g112)
    c: InternalAlignment(g114,g112)
    c: Block(g106)
    c: Block(g112)
    c: Coincident(g115,g106)
    c: Coincident(g115,g112)
    c: Vertical(g115)
    c: Coincident(g116,g112)
    c: Coincident(g116,g70)
    c: Coincident(g117,g70)
    c: Coincident(g117,g106)
    c: Weight(g118) = 1
    c: Equal(g118,g119)
    c: Equal(g118,g120)
    c: InternalAlignment(g118,g121)
    c: InternalAlignment(g119,g121)
    c: InternalAlignment(g120,g121)
    c: InternalAlignment(g122,g121)
    c: InternalAlignment(g123,g121)
    c: Weight(g124) = 1
    c: Equal(g124,g125)
    c: Equal(g124,g126)
    c: InternalAlignment(g124,g127)
    c: InternalAlignment(g125,g127)
    c: InternalAlignment(g126,g127)
    c: InternalAlignment(g128,g127)
    c: InternalAlignment(g129,g127)
    c: Block(g121)
    c: Block(g127)
    c: Coincident(g130,g121)
    c: Coincident(g130,g127)
    c: Vertical(g130)
    c: Coincident(g131,g127)
    c: Coincident(g131,g64)
    c: Coincident(g132,g64)
    c: Coincident(g132,g121)
    c: Weight(g133) = 1
    c: Equal(g133,g134)
    c: Equal(g133,g135)
    c: InternalAlignment(g133,g136)
    c: InternalAlignment(g134,g136)
    c: InternalAlignment(g135,g136)
    c: InternalAlignment(g137,g136)
    c: InternalAlignment(g138,g136)
    c: Weight(g139) = 1
    c: Equal(g139,g140)
    c: Equal(g139,g141)
    c: InternalAlignment(g139,g142)
    c: InternalAlignment(g140,g142)
    c: InternalAlignment(g141,g142)
    c: InternalAlignment(g143,g142)
    c: InternalAlignment(g144,g142)
    c: Weight(g145) = 1
    c: Equal(g145,g146)
    c: Equal(g145,g147)
    c: InternalAlignment(g145,g148)
    c: InternalAlignment(g146,g148)
    c: InternalAlignment(g147,g148)
    c: InternalAlignment(g149,g148)
    c: InternalAlignment(g150,g148)
    c: Weight(g151) = 1
    c: Equal(g151,g152)
    c: Equal(g151,g153)
    c: InternalAlignment(g151,g154)
    c: InternalAlignment(g152,g154)
    c: InternalAlignment(g153,g154)
    c: InternalAlignment(g155,g154)
    c: InternalAlignment(g156,g154)
    c: Block(g154)
    c: Block(g148)
    c: Block(g142)
    c: Block(g136)
    c: Coincident(g157,g31)
    c: Coincident(g157,g154)
    c: Coincident(g158,g154)
    c: Coincident(g158,g148)
    c: Horizontal(g158)
    c: Coincident(g159,g148)
    c: Coincident(g159,g31)
    c: Vertical(g159)
    c: Coincident(g160,g25)
    c: Coincident(g160,g142)
    c: Vertical(g160)
    c: Coincident(g161,g142)
    c: Coincident(g161,g136)
    c: Horizontal(g161)
    c: Coincident(g162,g136)
    c: Coincident(g162,g25)
    c: Weight(g163) = 1
    c: Equal(g163,g164)
    c: Equal(g163,g165)
    c: InternalAlignment(g163,g166)
    c: InternalAlignment(g164,g166)
    c: InternalAlignment(g165,g166)
    c: InternalAlignment(g167,g166)
    c: InternalAlignment(g168,g166)
    c: Weight(g169) = 1
    c: Equal(g169,g170)
    c: Equal(g169,g171)
    c: InternalAlignment(g169,g172)
    c: InternalAlignment(g170,g172)
    c: InternalAlignment(g171,g172)
    c: InternalAlignment(g173,g172)
    c: InternalAlignment(g174,g172)
    c: Weight(g175) = 1
    c: Equal(g175,g176)
    c: Equal(g175,g177)
    c: InternalAlignment(g175,g178)
    c: InternalAlignment(g176,g178)
    c: InternalAlignment(g177,g178)
    c: InternalAlignment(g179,g178)
    c: InternalAlignment(g180,g178)
    c: Weight(g181) = 1
    c: Equal(g181,g182)
    c: Equal(g181,g183)
    c: InternalAlignment(g181,g184)
    c: InternalAlignment(g182,g184)
    c: InternalAlignment(g183,g184)
    c: InternalAlignment(g185,g184)
    c: InternalAlignment(g186,g184)
    c: Block(g184)
    c: Block(g178)
    c: Block(g172)
    c: Block(g166)
    c: Coincident(g187,g184)
    c: Coincident(g187,g178)
    c: Horizontal(g187)
    c: Coincident(g188,g178)
    c: Coincident(g188,g13)
    c: Vertical(g188)
    c: Coincident(g189,g19)
    c: Coincident(g189,g172)
    c: Vertical(g189)
    c: Coincident(g190,g172)
    c: Coincident(g190,g166)
    c: Horizontal(g190)
    c: Coincident(g191,g166)
    c: Coincident(g191,g19)
    c: Coincident(g192,g13)
    c: Weight(g193) = 1
    c: Equal(g193,g194)
    c: Equal(g193,g195)
    c: InternalAlignment(g193,g196)
    c: InternalAlignment(g194,g196)
    c: InternalAlignment(g195,g196)
    c: InternalAlignment(g197,g196)
    c: InternalAlignment(g198,g196)
    c: Weight(g199) = 1
    c: Equal(g199,g200)
    c: Equal(g199,g201)
    c: InternalAlignment(g199,g202)
    c: InternalAlignment(g200,g202)
    c: InternalAlignment(g201,g202)
    c: InternalAlignment(g203,g202)
    c: InternalAlignment(g204,g202)
    c: Block(g202)
    c: Block(g196)
    c: Coincident(g205,g202)
    c: Coincident(g205,g37)
    c: Coincident(g206,g37)
    c: Coincident(g206,g196)
    c: Coincident(g207,g196)
    c: Coincident(g207,g202)
    c: Vertical(g207)
    c: Weight(g208) = 1
    c: Equal(g208,g209)
    c: Equal(g208,g210)
    c: InternalAlignment(g208,g211)
    c: InternalAlignment(g209,g211)
    c: InternalAlignment(g210,g211)
    c: InternalAlignment(g212,g211)
    c: InternalAlignment(g213,g211)
    c: Weight(g214) = 1
    c: Equal(g214,g215)
    c: Equal(g214,g216)
    c: InternalAlignment(g214,g217)
    c: InternalAlignment(g215,g217)
    c: InternalAlignment(g216,g217)
    c: InternalAlignment(g218,g217)
    c: InternalAlignment(g219,g217)
    c: Block(g217)
    c: Block(g211)
    c: Coincident(g220,g211)
    c: Coincident(g220,g43)
    c: Coincident(g221,g43)
    c: Coincident(g221,g217)
    c: Coincident(g222,g217)
    c: Coincident(g222,g211)
    c: Vertical(g222)
    c: Horizontal(g223)
    c: Block(g223)
    c: Vertical(g224)
    c: Block(g224)
    c: Block(g225)
    c: Weight(g226) = 1
    c: Equal(g226,g227)
    c: Equal(g226,g228)
    c: InternalAlignment(g226,g229)
    c: InternalAlignment(g227,g229)
    c: InternalAlignment(g228,g229)
    c: InternalAlignment(g230,g229)
    c: InternalAlignment(g231,g229)
    c: Weight(g232) = 1
    c: Equal(g232,g233)
    c: Equal(g232,g234)
    c: InternalAlignment(g232,g235)
    c: InternalAlignment(g233,g235)
    c: InternalAlignment(g234,g235)
    c: InternalAlignment(g236,g235)
    c: InternalAlignment(g237,g235)
    c: Weight(g238) = 1
    c: Equal(g238,g239)
    c: Equal(g238,g240)
    c: InternalAlignment(g238,g241)
    c: InternalAlignment(g239,g241)
    c: InternalAlignment(g240,g241)
    c: InternalAlignment(g242,g241)
    c: InternalAlignment(g243,g241)
    c: Weight(g244) = 1
    c: Equal(g244,g245)
    c: Equal(g244,g246)
    c: InternalAlignment(g244,g247)
    c: InternalAlignment(g245,g247)
    c: InternalAlignment(g246,g247)
    c: InternalAlignment(g248,g247)
    c: InternalAlignment(g249,g247)
    c: Block(g229)
    c: Block(g235)
    c: Block(g241)
    c: Block(g247)
    c: Coincident(g250,g235)
    c: Coincident(g250,g229)
    c: Horizontal(g250)
    c: Block(g192)
    c: Weight(g251) = 1
    c: Equal(g251,g252)
    c: Equal(g251,g253)
    c: InternalAlignment(g251,g254)
    c: InternalAlignment(g252,g254)
    c: InternalAlignment(g253,g254)
    c: InternalAlignment(g255,g254)
    c: InternalAlignment(g256,g254)
    c: Weight(g257) = 1
    c: Equal(g257,g258)
    c: Equal(g257,g259)
    c: InternalAlignment(g257,g260)
    c: InternalAlignment(g258,g260)
    c: InternalAlignment(g259,g260)
    c: InternalAlignment(g261,g260)
    c: InternalAlignment(g262,g260)
    c: Block(g254)
    c: Block(g260)
    c: Coincident(g263,g254)
    c: Coincident(g263,g260)
    c: Weight(g264) = 1
    c: Equal(g264,g265)
    c: Equal(g264,g266)
    c: InternalAlignment(g264,g267)
    c: InternalAlignment(g265,g267)
    c: InternalAlignment(g266,g267)
    c: InternalAlignment(g268,g267)
    c: InternalAlignment(g269,g267)
    c: Weight(g270) = 1
    c: Equal(g270,g271)
    c: Equal(g270,g272)
    c: InternalAlignment(g270,g273)
    c: InternalAlignment(g271,g273)
    c: InternalAlignment(g272,g273)
    c: InternalAlignment(g274,g273)
    c: InternalAlignment(g275,g273)
    c: Weight(g276) = 1
    c: Equal(g276,g277)
    c: Equal(g276,g278)
    c: InternalAlignment(g276,g279)
    c: InternalAlignment(g277,g279)
    c: InternalAlignment(g278,g279)
    c: InternalAlignment(g280,g279)
    c: InternalAlignment(g281,g279)
    c: Block(g279)
    c: Block(g273)
    c: Block(g267)
    c: Coincident(g282,g273)
    c: Coincident(g282,g267)
    c: Coincident(g283,g267)
    c: Coincident(g283,g279)
    c: Vertical(g283)
    c: Coincident(g284,g279)
    c: Coincident(g284,g273)
    c: Horizontal(g284)
    c: Weight(g285) = 1
    c: Equal(g285,g286)
    c: InternalAlignment(g285,g287)
    c: InternalAlignment(g286,g287)
    c: InternalAlignment(g288,g287)
    c: InternalAlignment(g289,g287)
    c: Weight(g290) = 1
    c: InternalAlignment(g291,g293)
    c: InternalAlignment(g292,g293)
    c: InternalAlignment(g294,g293)
    c: InternalAlignment(g295,g293)
    c: Weight(g296) = 1
    c: Equal(g296,g297)
    c: Equal(g296,g298)
    c: InternalAlignment(g296,g299)
    c: InternalAlignment(g297,g299)
    c: InternalAlignment(g298,g299)
    c: InternalAlignment(g300,g299)
    c: InternalAlignment(g301,g299)
    c: Equal(g302,g303)
    c: Equal(g302,g304)
    c: InternalAlignment(g302,g305)
    c: InternalAlignment(g303,g305)
    c: InternalAlignment(g304,g305)
    c: InternalAlignment(g306,g305)
    c: InternalAlignment(g307,g305)
    c: Block(g293)
    c: Block(g299)
    c: Block(g305)
    c: Block(g287)
    c: Coincident(g308,g287)
    c: Coincident(g308,g293)
    c: Horizontal(g308)
    c: Coincident(g309,g293)
    c: Coincident(g309,g299)
    c: Vertical(g309)
    c: Coincident(g310,g299)
    c: Coincident(g310,g305)
    c: Horizontal(g310)
    c: Coincident(g311,g305)
    c: Coincident(g311,g287)
    c: Weight(g312) = 1
    c: Equal(g312,g313)
    c: Equal(g312,g314)
    c: InternalAlignment(g312,g315)
    c: InternalAlignment(g313,g315)
    c: InternalAlignment(g314,g315)
    c: InternalAlignment(g316,g315)
    c: InternalAlignment(g317,g315)
    c: Weight(g318) = 1
    c: Equal(g318,g319)
    c: Equal(g318,g320)
    c: InternalAlignment(g318,g321)
    c: InternalAlignment(g319,g321)
    c: InternalAlignment(g320,g321)
    c: InternalAlignment(g322,g321)
    c: InternalAlignment(g323,g321)
    c: Weight(g324) = 1
    c: Equal(g324,g325)
    c: Equal(g324,g326)
    c: InternalAlignment(g324,g327)
    c: InternalAlignment(g325,g327)
    c: InternalAlignment(g326,g327)
    c: InternalAlignment(g328,g327)
    c: InternalAlignment(g329,g327)
    c: Block(g327)
    c: Block(g321)
    c: Block(g315)
    c: Coincident(g330,g327)
    c: Coincident(g330,g321)
    c: Horizontal(g330)
    c: Coincident(g331,g321)
    c: Coincident(g331,g315)
    c: Vertical(g331)
    c: Coincident(g332,g315)
    c: Coincident(g332,g327)
    c: InternalAlignment(g333,g334)
    c: InternalAlignment(g335,g334)
    c: InternalAlignment(g336,g334)
    c: Block(g334)
    c: Equal(g337,g338)
    c: Equal(g337,g339)
    c: InternalAlignment(g337,g340)
    c: InternalAlignment(g338,g340)
    c: InternalAlignment(g339,g340)
    c: InternalAlignment(g341,g340)
    c: InternalAlignment(g342,g340)
    c: Block(g340)
    c: Coincident(g343,g334)
    c: Horizontal(g343)
    c: Block(g343)
    c: Coincident(g344,g334)
    c: Coincident(g344,g260)
    c: Vertical(g344)
    c: Coincident(g345,g340)
    c: Coincident(g345,g254)
    c: Vertical(g345)
    c: Coincident(g347,g5)
    c: Coincident(g348,g5)
    c: Block(g346)
    c: Block(g5)
    c: Block(g348)
    c: Block(g347)
    c: Distance(g344) = 119.89
FEATURE [Sketcher::SketchObject] Sketch001
  FullyConstrained = true
  MapMode = 4
  Placement = pos=(0,0,0) rot=(0.57735,0.57735,0.57735;2.0944rad)
  Support = -> [Sketch]
  sketch-geometry (46):
    g0: BSplineCurve PolesCount=3 KnotsCount=2 Degree=2 IsPeriodic=0
    g1: ArcOfCircle CenterX=73.1223 CenterY=-32.291 CenterZ=0 NormalX=0 NormalY=0 NormalZ=1 AngleXU=0 Radius=13 StartAngle=5.92268 EndAngle=9.06428
    g2: ArcOfCircle CenterX=66.7816 CenterY=-49.1439 CenterZ=0 NormalX=0 NormalY=0 NormalZ=1 AngleXU=0 Radius=13 StartAngle=2.78068 EndAngle=5.92131
    g3: ArcOfCircle CenterX=55.9263 CenterY=-78.1807 CenterZ=0 NormalX=0 NormalY=0 NormalZ=1 AngleXU=0 Radius=13 StartAngle=5.92268 EndAngle=9.06428
    g4: ArcOfCircle CenterX=49.5884 CenterY=-95.0342 CenterZ=0 NormalX=0 NormalY=0 NormalZ=1 AngleXU=0 Radius=13 StartAngle=2.78068 EndAngle=5.92131
    g5: ArcOfCircle CenterX=38.7206 CenterY=-124.067 CenterZ=0 NormalX=0 NormalY=0 NormalZ=1 AngleXU=0 Radius=13 StartAngle=5.92268 EndAngle=9.06428
    g6: ArcOfCircle CenterX=32.3875 CenterY=-140.92 CenterZ=0 NormalX=0 NormalY=0 NormalZ=1 AngleXU=0 Radius=13 StartAngle=2.78068 EndAngle=5.92131
    g7: ArcOfCircle CenterX=21.4715 CenterY=-169.934 CenterZ=0 NormalX=0 NormalY=0 NormalZ=1 AngleXU=0 Radius=13 StartAngle=5.92268 EndAngle=9.06428
    g8: ArcOfCircle CenterX=15.1336 CenterY=-186.787 CenterZ=0 NormalX=0 NormalY=0 NormalZ=1 AngleXU=0 Radius=13 StartAngle=2.78068 EndAngle=5.92131
    g9-g12: Circle x4 (B-spline internal-alignment scaffolding for g13; pole/knot coordinates omitted)
    g13: BSplineCurve PolesCount=4 KnotsCount=2 Degree=3 IsPeriodic=0
    g14: GeomPoint X=28.8094 Y=-19.0875 Z=0
    g15: GeomPoint X=47.0443 Y=-50.4712 Z=0
    g16: Circle CenterX=53.5586 CenterY=-23.2695 CenterZ=0 NormalX=0 NormalY=0 NormalZ=1 AngleXU=0 Radius=3.24518
    g17: Circle CenterX=-195.441 CenterY=-127.082 CenterZ=0 NormalX=0 NormalY=0 NormalZ=1 AngleXU=0 Radius=1
    g18: Circle CenterX=-8.24091 CenterY=-197.481 CenterZ=0 NormalX=0 NormalY=0 NormalZ=1 AngleXU=0 Radius=1
    g19: Circle CenterX=12.8789 CenterY=-141.321 CenterZ=0 NormalX=0 NormalY=0 NormalZ=1 AngleXU=0 Radius=1
    g20: BSplineCurve PolesCount=3 KnotsCount=2 Degree=2 IsPeriodic=0
    g21: GeomPoint X=-195.441 Y=-127.082 Z=0
    g22: GeomPoint X=12.8789 Y=-141.321 Z=0
    g23: Circle CenterX=-12.8016 CenterY=-179.036 CenterZ=0 NormalX=0 NormalY=0 NormalZ=1 AngleXU=0 Radius=10.5072
    g24: Circle CenterX=0.933922 CenterY=-166.43 CenterZ=0 NormalX=0 NormalY=0 NormalZ=1 AngleXU=0 Radius=3.26661
    g25: Circle CenterX=-33.5518 CenterY=-176.44 CenterZ=0 NormalX=0 NormalY=0 NormalZ=1 AngleXU=0 Radius=5.64388
    g26: Circle CenterX=-47.2366 CenterY=-173.859 CenterZ=0 NormalX=0 NormalY=0 NormalZ=1 AngleXU=0 Radius=3.01653
    g27: Circle CenterX=-56.2595 CenterY=-171.456 CenterZ=0 NormalX=0 NormalY=0 NormalZ=1 AngleXU=0 Radius=2.12826
    g28: ArcOfCircle CenterX=51.2151 CenterY=-198.473 CenterZ=0 NormalX=0 NormalY=0 NormalZ=1 AngleXU=0 Radius=20 StartAngle=2.78189 EndAngle=4.35269
    g29: LineSegment StartX=32.4951 StartY=-191.433 StartZ=0 EndX=94.6578 EndY=-26.1352 EndZ=0
    g30: LineSegment StartX=43.1192 StartY=-220.001 StartZ=0 EndX=-196.497 EndY=-129.89 EndZ=0
    g31: LineSegment StartX=43.1192 StartY=-220.001 StartZ=0 EndX=44.1752 EndY=-217.193 EndZ=0
    g32: LineSegment StartX=117.223 StartY=-19.0875 StartZ=0 EndX=117.223 EndY=-16.0875 EndZ=0
    g33: LineSegment StartX=117.223 StartY=-16.0875 StartZ=0 EndX=17.2232 EndY=-16.0875 EndZ=0
    g34: LineSegment StartX=17.2232 StartY=-16.0875 StartZ=0 EndX=17.2232 EndY=-19.0875 EndZ=0
    g35: LineSegment StartX=28.8094 StartY=-19.0875 StartZ=0 EndX=17.2232 EndY=-19.0875 EndZ=0
    g36: LineSegment StartX=47.0443 StartY=-50.4712 StartZ=0 EndX=12.8789 EndY=-141.321 EndZ=0
    g37: LineSegment StartX=-195.441 StartY=-127.082 StartZ=0 EndX=-196.497 EndY=-129.89 EndZ=0
    g38: LineSegment StartX=85.2866 StartY=-36.8766 StartZ=0 EndX=78.9396 EndY=-53.7463 EndZ=0
    g39: LineSegment StartX=60.9579 StartY=-27.7053 StartZ=0 EndX=54.6191 EndY=-44.5532 EndZ=0
    g40: LineSegment StartX=68.0907 StartY=-82.7664 StartZ=0 EndX=61.7465 EndY=-99.6365 EndZ=0
    g41: LineSegment StartX=43.7619 StartY=-73.595 StartZ=0 EndX=37.426 EndY=-90.4435 EndZ=0
    g42: LineSegment StartX=50.885 StartY=-128.652 StartZ=0 EndX=44.5456 EndY=-145.522 EndZ=0
    g43: LineSegment StartX=26.5562 StartY=-119.481 StartZ=0 EndX=20.2251 EndY=-136.329 EndZ=0
    g44: LineSegment StartX=9.3071 StartY=-165.349 StartZ=0 EndX=2.97115 EndY=-182.197 EndZ=0
    g45: LineSegment StartX=33.6358 StartY=-174.52 StartZ=0 EndX=27.2917 EndY=-191.39 EndZ=0
  constraints (71):
    c: Block(g0)
    c: Block(g1)
    c: Block(g2)
    c: Block(g4)
    c: Block(g3)
    c: Block(g6)
    c: Block(g5)
    c: Block(g8)
    c: Block(g7)
    c: Weight(g9) = 1
    c: Equal(g9,g10)
    c: Equal(g9,g11)
    c: Equal(g9,g12)
    c: InternalAlignment(g9-g12 -> g13) x4
    c: InternalAlignment(g14,g13)
    c: InternalAlignment(g15,g13)
    c: Block(g16)
    c: Weight(g17) = 1
    c: Equal(g17,g18)
    c: Equal(g17,g19)
    c: InternalAlignment(g17,g20)
    c: InternalAlignment(g18,g20)
    c: InternalAlignment(g19,g20)
    c: InternalAlignment(g21,g20)
    c: InternalAlignment(g22,g20)
    c: Block(g20)
    c: Block(g23)
    c: Block(g24)
    c: Block(g25)
    c: Block(g26)
    c: Block(g27)
    c: Block(g28)
    c: Coincident(g29,g28)
    c: Coincident(g29,g0)
    c: Block(g13)
    c: Coincident(g31,g30)
    c: Coincident(g31,g28)
    c: Block(g31)
    c: Coincident(g32,g0)
    c: Vertical(g32)
    c: Coincident(g33,g32)
    c: Horizontal(g33)
    c: Coincident(g34,g33)
    c: Vertical(g34)
    c: Block(g33)
    c: Coincident(g35,g13)
    c: Coincident(g35,g34)
    c: Horizontal(g35)
    c: Coincident(g36,g13)
    c: Coincident(g36,g20)
    c: Coincident(g37,g20)
    c: Coincident(g37,g30)
    c: Block(g30)
    c: Coincident(g38,g1)
    c: Coincident(g38,g2)
    c: Coincident(g39,g1)
    c: Coincident(g39,g2)
    c: Coincident(g40,g3)
    c: Coincident(g40,g4)
    c: Coincident(g41,g3)
    c: Coincident(g41,g4)
    c: Coincident(g42,g5)
    c: Coincident(g42,g6)
    c: Coincident(g43,g5)
    c: Coincident(g43,g6)
    c: Coincident(g44,g7)
    c: Coincident(g44,g8)
    c: Coincident(g45,g7)
    c: Coincident(g45,g8)
    c: Distance(g30) = 256
    c: Distance(g33) = 100
FEATURE [Part::Extrusion] Extrude002
  Base = -> Sketch001
  Dir = (1,0,0)
  DirMode = 2
  FaceMakerClass = Part::FaceMakerBullseye
  LengthFwd = 8
  LengthRev = 0
  Solid = true
  Symmetric = false
FEATURE [Sketcher::SketchObject] Sketch002
  FullyConstrained = true
  sketch-geometry (20):
    g0: LineSegment StartX=-2.77179 StartY=-200.304 StartZ=0 EndX=5.22821 EndY=-200.304 EndZ=0
    g1: LineSegment StartX=5.22821 StartY=-200.304 StartZ=0 EndX=5.22821 EndY=-197.304 EndZ=0
    g2: LineSegment StartX=-2.77179 StartY=-200.304 StartZ=0 EndX=-2.77179 EndY=-197.304 EndZ=0
    g3: LineSegment StartX=5.22821 StartY=-197.304 StartZ=0 EndX=8.22821 EndY=-197.304 EndZ=0
    g4: LineSegment StartX=-2.77179 StartY=-197.304 StartZ=0 EndX=-5.77179 EndY=-197.304 EndZ=0
    g5: LineSegment StartX=19.2282 StartY=-203.304 StartZ=0 EndX=19.2282 EndY=-206.304 EndZ=0
    g6: LineSegment StartX=-16.7718 StartY=-203.304 StartZ=0 EndX=-16.7718 EndY=-206.304 EndZ=0
    g7: LineSegment StartX=-16.7718 StartY=-206.304 StartZ=0 EndX=19.2282 EndY=-206.304 EndZ=0
    g8: Circle CenterX=-16.7718 CenterY=-203.304 CenterZ=0 NormalX=0 NormalY=0 NormalZ=1 AngleXU=0 Radius=1
    g9: Circle CenterX=-5.77179 CenterY=-203.304 CenterZ=0 NormalX=0 NormalY=0 NormalZ=1 AngleXU=0 Radius=1
    g10: Circle CenterX=-5.77179 CenterY=-197.304 CenterZ=0 NormalX=0 NormalY=0 NormalZ=1 AngleXU=0 Radius=1
    g11: BSplineCurve PolesCount=3 KnotsCount=2 Degree=2 IsPeriodic=0
    g12: GeomPoint X=-16.7718 Y=-203.304 Z=0
    g13: GeomPoint X=-5.77179 Y=-197.304 Z=0
    g14: Circle CenterX=19.2282 CenterY=-203.304 CenterZ=0 NormalX=0 NormalY=0 NormalZ=1 AngleXU=0 Radius=1
    g15: Circle CenterX=8.22821 CenterY=-203.304 CenterZ=0 NormalX=0 NormalY=0 NormalZ=1 AngleXU=0 Radius=1
    g16: Circle CenterX=8.22821 CenterY=-197.304 CenterZ=0 NormalX=0 NormalY=0 NormalZ=1 AngleXU=0 Radius=1
    g17: BSplineCurve PolesCount=3 KnotsCount=2 Degree=2 IsPeriodic=0
    g18: GeomPoint X=19.2282 Y=-203.304 Z=0
    g19: GeomPoint X=8.22821 Y=-197.304 Z=0
  constraints (41):
    c: Horizontal(g0)
    c: Distance(g0) = 8
    c: Coincident(g1,g0)
    c: Vertical(g1)
    c: Distance(g1) = 3
    c: Coincident(g2,g0)
    c: Vertical(g2)
    c: Distance(g2) = 3
    c: Coincident(g3,g1)
    c: Horizontal(g3)
    c: Distance(g3) = 3
    c: Coincident(g4,g2)
    c: Horizontal(g4)
    c: Distance(g4) = 3
    c: Vertical(g5)
    c: Vertical(g6)
    c: Coincident(g7,g6)
    c: Coincident(g7,g5)
    c: Weight(g8) = 1
    c: Equal(g8,g9)
    c: Equal(g8,g10)
    c: Coincident(g11,g4)
    c: InternalAlignment(g8,g11)
    c: InternalAlignment(g9,g11)
    c: InternalAlignment(g10,g11)
    c: InternalAlignment(g12,g11)
    c: InternalAlignment(g13,g11)
    c: Coincident(g17,g5)
    c: Weight(g14) = 1
    c: Equal(g14,g15)
    c: Equal(g14,g16)
    c: Coincident(g17,g3)
    c: InternalAlignment(g14,g17)
    c: InternalAlignment(g15,g17)
    c: InternalAlignment(g16,g17)
    c: InternalAlignment(g18,g17)
    c: InternalAlignment(g19,g17)
    c: Block(g7)
    c: Block(g17)
    c: Block(g11)
    c: Block(g6)
FEATURE [Part::Extrusion] Extrude003
  Base = -> Sketch002
  Dir = (0,0,1)
  DirMode = 2
  FaceMakerClass = Part::FaceMakerBullseye
  LengthFwd = 260
  LengthRev = 0
  Solid = true
  Symmetric = false
FEATURE [Sketcher::SketchObject] Sketch003
  FullyConstrained = false
  sketch-geometry (416):
    g0: LineSegment StartX=-42.9272 StartY=136.221 StartZ=0 EndX=-42.9272 EndY=-103.779 EndZ=0
    g1: LineSegment StartX=407.073 StartY=136.221 StartZ=0 EndX=407.073 EndY=-103.779 EndZ=0
    g2: ArcOfCircle CenterX=-26.9272 CenterY=-83.7794 CenterZ=0 NormalX=0 NormalY=0 NormalZ=1 AngleXU=0 Radius=8 StartAngle=3.14159 EndAngle=6.28319
    g3: ArcOfCircle CenterX=391.073 CenterY=-83.7794 CenterZ=0 NormalX=0 NormalY=0 NormalZ=1 AngleXU=0 Radius=8 StartAngle=3.14159 EndAngle=6.28319
    g4: Circle CenterX=175.022 CenterY=27.0628 CenterZ=0 NormalX=0 NormalY=0 NormalZ=1 AngleXU=0 Radius=1
    g5: Circle CenterX=179.022 CenterY=24.8665 CenterZ=0 NormalX=0 NormalY=0 NormalZ=1 AngleXU=0 Radius=1
    g6: Circle CenterX=179.022 CenterY=27.0628 CenterZ=0 NormalX=0 NormalY=0 NormalZ=1 AngleXU=0 Radius=1
    g7: BSplineCurve PolesCount=3 KnotsCount=2 Degree=2 IsPeriodic=0
    g8: GeomPoint X=175.022 Y=27.0628 Z=0
    g9: GeomPoint X=179.022 Y=27.0628 Z=0
    g10: Circle CenterX=189.124 CenterY=27.0628 CenterZ=0 NormalX=0 NormalY=0 NormalZ=1 AngleXU=0 Radius=1
    g11: Circle CenterX=185.124 CenterY=24.8665 CenterZ=0 NormalX=0 NormalY=0 NormalZ=1 AngleXU=0 Radius=1
    g12: Circle CenterX=185.124 CenterY=27.0628 CenterZ=0 NormalX=0 NormalY=0 NormalZ=1 AngleXU=0 Radius=1
    g13: BSplineCurve PolesCount=3 KnotsCount=2 Degree=2 IsPeriodic=0
    g14: GeomPoint X=189.124 Y=27.0628 Z=0
    g15: GeomPoint X=185.124 Y=27.0628 Z=0
    g16: Circle CenterX=175.022 CenterY=5.37834 CenterZ=0 NormalX=0 NormalY=0 NormalZ=1 AngleXU=0 Radius=1
    g17: Circle CenterX=179.022 CenterY=7.57463 CenterZ=0 NormalX=0 NormalY=0 NormalZ=1 AngleXU=0 Radius=1
    g18: Circle CenterX=179.022 CenterY=5.34704 CenterZ=0 NormalX=0 NormalY=0 NormalZ=1 AngleXU=0 Radius=1
    g19: BSplineCurve PolesCount=3 KnotsCount=2 Degree=2 IsPeriodic=0
    g20: GeomPoint X=175.022 Y=5.37834 Z=0
    g21: GeomPoint X=179.022 Y=5.34704 Z=0
    g22: Circle CenterX=189.124 CenterY=5.37834 CenterZ=0 NormalX=0 NormalY=0 NormalZ=1 AngleXU=0 Radius=1
    g23: Circle CenterX=185.124 CenterY=7.57463 CenterZ=0 NormalX=0 NormalY=0 NormalZ=1 AngleXU=0 Radius=1
    g24: Circle CenterX=185.124 CenterY=5.34704 CenterZ=0 NormalX=0 NormalY=0 NormalZ=1 AngleXU=0 Radius=1
    g25: BSplineCurve PolesCount=3 KnotsCount=2 Degree=2 IsPeriodic=0
    g26: GeomPoint X=189.124 Y=5.37834 Z=0
    g27: GeomPoint X=185.124 Y=5.34704 Z=0
    g28: Circle CenterX=165.871 CenterY=18.1458 CenterZ=0 NormalX=0 NormalY=0 NormalZ=1 AngleXU=0 Radius=1
    g29: Circle CenterX=169.377 CenterY=16.2206 CenterZ=0 NormalX=0 NormalY=0 NormalZ=1 AngleXU=0 Radius=1
    g30: Circle CenterX=165.871 CenterY=14.2954 CenterZ=0 NormalX=0 NormalY=0 NormalZ=1 AngleXU=0 Radius=1
    g31: BSplineCurve PolesCount=3 KnotsCount=2 Degree=2 IsPeriodic=0
    g32: GeomPoint X=165.871 Y=18.1458 Z=0
    g33: GeomPoint X=165.871 Y=14.2954 Z=0
    g34: Circle CenterX=198.275 CenterY=18.1458 CenterZ=0 NormalX=0 NormalY=0 NormalZ=1 AngleXU=0 Radius=1
    g35: Circle CenterX=194.768 CenterY=16.2206 CenterZ=0 NormalX=0 NormalY=0 NormalZ=1 AngleXU=0 Radius=1
    g36: Circle CenterX=198.275 CenterY=14.2954 CenterZ=0 NormalX=0 NormalY=0 NormalZ=1 AngleXU=0 Radius=1
    g37: BSplineCurve PolesCount=3 KnotsCount=2 Degree=2 IsPeriodic=0
    g38: GeomPoint X=198.275 Y=18.1458 Z=0
    g39: GeomPoint X=198.275 Y=14.2954 Z=0
    g40: LineSegment StartX=407.073 StartY=-103.779 StartZ=0 EndX=-42.9272 EndY=-103.779 EndZ=0
    g41: Circle CenterX=125.607 CenterY=54.1951 CenterZ=0 NormalX=0 NormalY=0 NormalZ=1 AngleXU=0 Radius=1
    g42: Circle CenterX=139.632 CenterY=46.4944 CenterZ=0 NormalX=0 NormalY=0 NormalZ=1 AngleXU=0 Radius=1
    g43: Circle CenterX=127.326 CenterY=56.7187 CenterZ=0 NormalX=0 NormalY=0 NormalZ=1 AngleXU=0 Radius=1
    g44: BSplineCurve PolesCount=3 KnotsCount=2 Degree=2 IsPeriodic=0
    g45: GeomPoint X=125.607 Y=54.1951 Z=0
    g46: GeomPoint X=127.326 Y=56.7187 Z=0
    g47: Circle CenterX=236.821 CenterY=56.7187 CenterZ=0 NormalX=0 NormalY=0 NormalZ=1 AngleXU=0 Radius=1
    g48: Circle CenterX=224.513 CenterY=46.4944 CenterZ=0 NormalX=0 NormalY=0 NormalZ=1 AngleXU=0 Radius=1
    g49: Circle CenterX=238.538 CenterY=54.1951 CenterZ=0 NormalX=0 NormalY=0 NormalZ=1 AngleXU=0 Radius=1
    g50: BSplineCurve PolesCount=3 KnotsCount=2 Degree=2 IsPeriodic=0
    g51: GeomPoint X=236.821 Y=56.7187 Z=0
    g52: GeomPoint X=238.538 Y=54.1951 Z=0
    g53: Circle CenterX=238.538 CenterY=-21.7539 CenterZ=0 NormalX=0 NormalY=0 NormalZ=1 AngleXU=0 Radius=1
    g54: Circle CenterX=224.513 CenterY=-14.0532 CenterZ=0 NormalX=0 NormalY=0 NormalZ=1 AngleXU=0 Radius=1
    g55: Circle CenterX=236.821 CenterY=-24.2775 CenterZ=0 NormalX=0 NormalY=0 NormalZ=1 AngleXU=0 Radius=1
    g56: BSplineCurve PolesCount=3 KnotsCount=2 Degree=2 IsPeriodic=0
    g57: GeomPoint X=238.538 Y=-21.7539 Z=0
    g58: GeomPoint X=236.821 Y=-24.2775 Z=0
    g59: Circle CenterX=125.607 CenterY=-21.7539 CenterZ=0 NormalX=0 NormalY=0 NormalZ=1 AngleXU=0 Radius=1
    g60: Circle CenterX=139.632 CenterY=-14.0532 CenterZ=0 NormalX=0 NormalY=0 NormalZ=1 AngleXU=0 Radius=1
    g61: Circle CenterX=127.325 CenterY=-24.2775 CenterZ=0 NormalX=0 NormalY=0 NormalZ=1 AngleXU=0 Radius=1
    g62: BSplineCurve PolesCount=3 KnotsCount=2 Degree=2 IsPeriodic=0
    g63: GeomPoint X=125.607 Y=-21.7539 Z=0
    g64: GeomPoint X=127.325 Y=-24.2775 Z=0
    g65: Circle CenterX=302.996 CenterY=111.695 CenterZ=0 NormalX=0 NormalY=0 NormalZ=1 AngleXU=0 Radius=1
    g66: Circle CenterX=306.073 CenterY=114.251 CenterZ=0 NormalX=0 NormalY=0 NormalZ=1 AngleXU=0 Radius=1
    g67: Circle CenterX=306.073 CenterY=110.251 CenterZ=0 NormalX=0 NormalY=0 NormalZ=1 AngleXU=0 Radius=1
    g68: BSplineCurve PolesCount=3 KnotsCount=2 Degree=2 IsPeriodic=0
    g69: GeomPoint X=302.996 Y=111.695 Z=0
    g70: GeomPoint X=306.073 Y=110.251 Z=0
    g71: Circle CenterX=306.073 CenterY=95.2763 CenterZ=0 NormalX=0 NormalY=0 NormalZ=1 AngleXU=0 Radius=1
    g72: Circle CenterX=306.073 CenterY=91.2763 CenterZ=0 NormalX=0 NormalY=0 NormalZ=1 AngleXU=0 Radius=1
    g73: Circle CenterX=302.567 CenterY=89.3511 CenterZ=0 NormalX=0 NormalY=0 NormalZ=1 AngleXU=0 Radius=1
    g74: BSplineCurve PolesCount=3 KnotsCount=2 Degree=2 IsPeriodic=0
    g75: GeomPoint X=306.073 Y=95.2763 Z=0
    g76: GeomPoint X=302.567 Y=89.3511 Z=0
    g77: LineSegment StartX=306.073 StartY=110.251 StartZ=0 EndX=306.073 EndY=95.2763 EndZ=0
    g78: LineSegment StartX=302.996 StartY=111.695 StartZ=0 EndX=236.821 EndY=56.7187 EndZ=0
    g79: LineSegment StartX=238.538 StartY=54.1951 StartZ=0 EndX=302.567 EndY=89.3511 EndZ=0
    g80: Circle CenterX=61.1496 CenterY=111.695 CenterZ=0 NormalX=0 NormalY=0 NormalZ=1 AngleXU=0 Radius=1
    g81: Circle CenterX=58.0728 CenterY=114.251 CenterZ=0 NormalX=0 NormalY=0 NormalZ=1 AngleXU=0 Radius=1
    g82: Circle CenterX=58.0728 CenterY=110.251 CenterZ=0 NormalX=0 NormalY=0 NormalZ=1 AngleXU=0 Radius=1
    g83: BSplineCurve PolesCount=3 KnotsCount=2 Degree=2 IsPeriodic=0
    g84: GeomPoint X=61.1496 Y=111.695 Z=0
    g85: GeomPoint X=58.0728 Y=110.251 Z=0
    g86: Circle CenterX=61.5791 CenterY=89.3511 CenterZ=0 NormalX=0 NormalY=0 NormalZ=1 AngleXU=0 Radius=1
    g87: Circle CenterX=58.0728 CenterY=91.2763 CenterZ=0 NormalX=0 NormalY=0 NormalZ=1 AngleXU=0 Radius=1
    g88: Circle CenterX=58.0728 CenterY=95.2763 CenterZ=0 NormalX=0 NormalY=0 NormalZ=1 AngleXU=0 Radius=1
    g89: BSplineCurve PolesCount=3 KnotsCount=2 Degree=2 IsPeriodic=0
    g90: GeomPoint X=61.5791 Y=89.3511 Z=0
    g91: GeomPoint X=58.0728 Y=95.2763 Z=0
    g92: LineSegment StartX=58.0728 StartY=110.251 StartZ=0 EndX=58.0728 EndY=95.2763 EndZ=0
    g93: LineSegment StartX=61.1496 StartY=111.695 StartZ=0 EndX=127.326 EndY=56.7187 EndZ=0
    g94: LineSegment StartX=125.607 StartY=54.1951 StartZ=0 EndX=61.5791 EndY=89.3511 EndZ=0
    g95: Circle CenterX=61.5791 CenterY=-56.9099 CenterZ=0 NormalX=0 NormalY=0 NormalZ=1 AngleXU=0 Radius=1
    g96: Circle CenterX=58.0728 CenterY=-58.8351 CenterZ=0 NormalX=0 NormalY=0 NormalZ=1 AngleXU=0 Radius=1
    g97: Circle CenterX=58.0728 CenterY=-62.8351 CenterZ=0 NormalX=0 NormalY=0 NormalZ=1 AngleXU=0 Radius=1
    g98: BSplineCurve PolesCount=3 KnotsCount=2 Degree=2 IsPeriodic=0
    g99: GeomPoint X=61.5791 Y=-56.9099 Z=0
    g100: GeomPoint X=58.0728 Y=-62.8351 Z=0
    g101: Circle CenterX=58.0728 CenterY=-77.8102 CenterZ=0 NormalX=0 NormalY=0 NormalZ=1 AngleXU=0 Radius=1
    g102: Circle CenterX=58.0728 CenterY=-81.8102 CenterZ=0 NormalX=0 NormalY=0 NormalZ=1 AngleXU=0 Radius=1
    g103: Circle CenterX=61.1496 CenterY=-79.2541 CenterZ=0 NormalX=0 NormalY=0 NormalZ=1 AngleXU=0 Radius=1
    g104: BSplineCurve PolesCount=3 KnotsCount=2 Degree=2 IsPeriodic=0
    g105: GeomPoint X=58.0728 Y=-77.8102 Z=0
    g106: GeomPoint X=61.1496 Y=-79.2541 Z=0
    g107: LineSegment StartX=58.0728 StartY=-62.8351 StartZ=0 EndX=58.0728 EndY=-77.8102 EndZ=0
    g108: LineSegment StartX=61.1496 StartY=-79.2541 StartZ=0 EndX=127.325 EndY=-24.2775 EndZ=0
    g109: LineSegment StartX=125.607 StartY=-21.7539 StartZ=0 EndX=61.5791 EndY=-56.9099 EndZ=0
    g110: Circle CenterX=302.567 CenterY=-56.9099 CenterZ=0 NormalX=0 NormalY=0 NormalZ=1 AngleXU=0 Radius=1
    g111: Circle CenterX=306.073 CenterY=-58.8351 CenterZ=0 NormalX=0 NormalY=0 NormalZ=1 AngleXU=0 Radius=1
    g112: Circle CenterX=306.073 CenterY=-62.8351 CenterZ=0 NormalX=0 NormalY=0 NormalZ=1 AngleXU=0 Radius=1
    g113: BSplineCurve PolesCount=3 KnotsCount=2 Degree=2 IsPeriodic=0
    g114: GeomPoint X=302.567 Y=-56.9099 Z=0
    g115: GeomPoint X=306.073 Y=-62.8351 Z=0
    g116: Circle CenterX=302.996 CenterY=-79.2541 CenterZ=0 NormalX=0 NormalY=0 NormalZ=1 AngleXU=0 Radius=1
    g117: Circle CenterX=306.073 CenterY=-81.8102 CenterZ=0 NormalX=0 NormalY=0 NormalZ=1 AngleXU=0 Radius=1
    g118: Circle CenterX=306.073 CenterY=-77.8102 CenterZ=0 NormalX=0 NormalY=0 NormalZ=1 AngleXU=0 Radius=1
    g119: BSplineCurve PolesCount=3 KnotsCount=2 Degree=2 IsPeriodic=0
    g120: GeomPoint X=302.996 Y=-79.2541 Z=0
    g121: GeomPoint X=306.073 Y=-77.8102 Z=0
    g122: LineSegment StartX=306.073 StartY=-62.8351 StartZ=0 EndX=306.073 EndY=-77.8102 EndZ=0
    g123: LineSegment StartX=302.996 StartY=-79.2541 StartZ=0 EndX=236.821 EndY=-24.2775 EndZ=0
    g124: LineSegment StartX=238.538 StartY=-21.7539 StartZ=0 EndX=302.567 EndY=-56.9099 EndZ=0
    g125: Circle CenterX=61.6457 CenterY=-88.8112 CenterZ=0 NormalX=0 NormalY=0 NormalZ=1 AngleXU=0 Radius=1
    g126: Circle CenterX=58.0728 CenterY=-91.7794 CenterZ=0 NormalX=0 NormalY=0 NormalZ=1 AngleXU=0 Radius=1
    g127: Circle CenterX=63.9135 CenterY=-91.7791 CenterZ=0 NormalX=0 NormalY=0 NormalZ=1 AngleXU=0 Radius=1
    g128: BSplineCurve PolesCount=3 KnotsCount=2 Degree=2 IsPeriodic=0
    g129: GeomPoint X=61.6457 Y=-88.8112 Z=0
    g130: GeomPoint X=63.9135 Y=-91.7791 Z=0
    g131: Circle CenterX=179.022 CenterY=-85.8163 CenterZ=0 NormalX=0 NormalY=0 NormalZ=1 AngleXU=0 Radius=1
    g132: Circle CenterX=179.022 CenterY=-91.7794 CenterZ=0 NormalX=0 NormalY=0 NormalZ=1 AngleXU=0 Radius=1
    g133: Circle CenterX=171.895 CenterY=-91.7791 CenterZ=0 NormalX=0 NormalY=0 NormalZ=1 AngleXU=0 Radius=1
    g134: BSplineCurve PolesCount=3 KnotsCount=2 Degree=2 IsPeriodic=0
    g135: GeomPoint X=179.022 Y=-85.8163 Z=0
    g136: GeomPoint X=171.895 Y=-91.7791 Z=0
    g137: Circle CenterX=185.124 CenterY=-86.2028 CenterZ=0 NormalX=0 NormalY=0 NormalZ=1 AngleXU=0 Radius=1
    g138: Circle CenterX=185.124 CenterY=-91.7794 CenterZ=0 NormalX=0 NormalY=0 NormalZ=1 AngleXU=0 Radius=1
    g139: Circle CenterX=191.747 CenterY=-91.7794 CenterZ=0 NormalX=0 NormalY=0 NormalZ=1 AngleXU=0 Radius=1
    g140: BSplineCurve PolesCount=3 KnotsCount=2 Degree=2 IsPeriodic=0
    g141: GeomPoint X=185.124 Y=-86.2028 Z=0
    g142: GeomPoint X=191.747 Y=-91.7794 Z=0
    g143: Circle CenterX=299.888 CenterY=-86.6413 CenterZ=0 NormalX=0 NormalY=0 NormalZ=1 AngleXU=0 Radius=1
    g144: Circle CenterX=306.073 CenterY=-91.7794 CenterZ=0 NormalX=0 NormalY=0 NormalZ=1 AngleXU=0 Radius=1
    g145: Circle CenterX=298.776 CenterY=-91.7794 CenterZ=0 NormalX=0 NormalY=0 NormalZ=1 AngleXU=0 Radius=1
    g146: BSplineCurve PolesCount=3 KnotsCount=2 Degree=2 IsPeriodic=0
    g147: GeomPoint X=299.888 Y=-86.6413 Z=0
    g148: GeomPoint X=298.776 Y=-91.7794 Z=0
    g149: LineSegment StartX=189.124 StartY=5.37834 StartZ=0 EndX=299.888 EndY=-86.6413 EndZ=0
    g150: LineSegment StartX=298.776 StartY=-91.7794 StartZ=0 EndX=191.747 EndY=-91.7794 EndZ=0
    g151: LineSegment StartX=185.124 StartY=-86.2028 StartZ=0 EndX=185.124 EndY=5.34704 EndZ=0
    g152: LineSegment StartX=179.022 StartY=5.34704 StartZ=0 EndX=179.022 EndY=-85.8163 EndZ=0
    g153: LineSegment StartX=171.895 StartY=-91.7791 StartZ=0 EndX=63.9135 EndY=-91.7791 EndZ=0
    g154: LineSegment StartX=61.6457 StartY=-88.8112 StartZ=0 EndX=175.022 EndY=5.37834 EndZ=0
    g155: Circle CenterX=302.073 CenterY=124.221 CenterZ=0 NormalX=0 NormalY=0 NormalZ=1 AngleXU=0 Radius=1
    g156: Circle CenterX=306.073 CenterY=124.221 CenterZ=0 NormalX=0 NormalY=0 NormalZ=1 AngleXU=0 Radius=1
    g157: Circle CenterX=302.996 CenterY=121.665 CenterZ=0 NormalX=0 NormalY=0 NormalZ=1 AngleXU=0 Radius=1
    g158: BSplineCurve PolesCount=3 KnotsCount=2 Degree=2 IsPeriodic=0
    g159: GeomPoint X=302.073 Y=124.221 Z=0
    g160: GeomPoint X=302.996 Y=121.665 Z=0
    g161: Circle CenterX=189.124 CenterY=124.221 CenterZ=0 NormalX=0 NormalY=0 NormalZ=1 AngleXU=0 Radius=1
    g162: Circle CenterX=185.124 CenterY=124.221 CenterZ=0 NormalX=0 NormalY=0 NormalZ=1 AngleXU=0 Radius=1
    g163: Circle CenterX=185.124 CenterY=120.221 CenterZ=0 NormalX=0 NormalY=0 NormalZ=1 AngleXU=0 Radius=1
    g164: BSplineCurve PolesCount=3 KnotsCount=2 Degree=2 IsPeriodic=0
    g165: GeomPoint X=189.124 Y=124.221 Z=0
    g166: GeomPoint X=185.124 Y=120.221 Z=0
    g167: Circle CenterX=175.022 CenterY=124.221 CenterZ=0 NormalX=0 NormalY=0 NormalZ=1 AngleXU=0 Radius=1
    g168: Circle CenterX=179.022 CenterY=124.221 CenterZ=0 NormalX=0 NormalY=0 NormalZ=1 AngleXU=0 Radius=1
    g169: Circle CenterX=179.022 CenterY=120.221 CenterZ=0 NormalX=0 NormalY=0 NormalZ=1 AngleXU=0 Radius=1
    g170: BSplineCurve PolesCount=3 KnotsCount=2 Degree=2 IsPeriodic=0
    g171: GeomPoint X=175.022 Y=124.221 Z=0
    g172: GeomPoint X=179.022 Y=120.221 Z=0
    g173: Circle CenterX=62.0728 CenterY=124.221 CenterZ=0 NormalX=0 NormalY=0 NormalZ=1 AngleXU=0 Radius=1
    g174: Circle CenterX=58.0728 CenterY=124.221 CenterZ=0 NormalX=0 NormalY=0 NormalZ=1 AngleXU=0 Radius=1
    g175: Circle CenterX=61.1496 CenterY=121.665 CenterZ=0 NormalX=0 NormalY=0 NormalZ=1 AngleXU=0 Radius=1
    g176: BSplineCurve PolesCount=3 KnotsCount=2 Degree=2 IsPeriodic=0
    g177: GeomPoint X=62.0728 Y=124.221 Z=0
    g178: GeomPoint X=61.1496 Y=121.665 Z=0
    g179: LineSegment StartX=179.022 StartY=120.221 StartZ=0 EndX=179.022 EndY=27.0628 EndZ=0
    g180: LineSegment StartX=185.124 StartY=27.0628 StartZ=0 EndX=185.124 EndY=120.221 EndZ=0
    g181: LineSegment StartX=302.996 StartY=121.665 StartZ=0 EndX=189.124 EndY=27.0628 EndZ=0
    g182: LineSegment StartX=175.022 StartY=27.0628 StartZ=0 EndX=61.1496 EndY=121.665 EndZ=0
    g183: Circle CenterX=61.5791 CenterY=75.4095 CenterZ=0 NormalX=0 NormalY=0 NormalZ=1 AngleXU=0 Radius=1
    g184: Circle CenterX=58.0728 CenterY=77.3346 CenterZ=0 NormalX=0 NormalY=0 NormalZ=1 AngleXU=0 Radius=1
    g185: Circle CenterX=58.0728 CenterY=73.3346 CenterZ=0 NormalX=0 NormalY=0 NormalZ=1 AngleXU=0 Radius=1
    g186: BSplineCurve PolesCount=3 KnotsCount=2 Degree=2 IsPeriodic=0
    g187: GeomPoint X=61.5791 Y=75.4095 Z=0
    g188: GeomPoint X=58.0728 Y=73.3346 Z=0
    g189: Circle CenterX=58.0728 CenterY=-40.8935 CenterZ=0 NormalX=0 NormalY=0 NormalZ=1 AngleXU=0 Radius=1
    g190: Circle CenterX=58.0728 CenterY=-44.8935 CenterZ=0 NormalX=0 NormalY=0 NormalZ=1 AngleXU=0 Radius=1
    g191: Circle CenterX=61.5791 CenterY=-42.9683 CenterZ=0 NormalX=0 NormalY=0 NormalZ=1 AngleXU=0 Radius=1
    g192: BSplineCurve PolesCount=3 KnotsCount=2 Degree=2 IsPeriodic=0
    g193: GeomPoint X=58.0728 Y=-40.8935 Z=0
    g194: GeomPoint X=61.5791 Y=-42.9683 Z=0
    g195: LineSegment StartX=61.5791 StartY=-42.9683 StartZ=0 EndX=165.871 EndY=14.2954 EndZ=0
    g196: LineSegment StartX=165.871 StartY=18.1458 StartZ=0 EndX=61.5791 EndY=75.4095 EndZ=0
    g197: LineSegment StartX=58.0728 StartY=73.3346 StartZ=0 EndX=58.0728 EndY=-40.8935 EndZ=0
    g198: Circle CenterX=302.567 CenterY=-42.9683 CenterZ=0 NormalX=0 NormalY=0 NormalZ=1 AngleXU=0 Radius=1
    g199: Circle CenterX=306.073 CenterY=-44.8935 CenterZ=0 NormalX=0 NormalY=0 NormalZ=1 AngleXU=0 Radius=1
    g200: Circle CenterX=306.073 CenterY=-40.8935 CenterZ=0 NormalX=0 NormalY=0 NormalZ=1 AngleXU=0 Radius=1
    g201: BSplineCurve PolesCount=3 KnotsCount=2 Degree=2 IsPeriodic=0
    g202: GeomPoint X=302.567 Y=-42.9683 Z=0
    g203: GeomPoint X=306.073 Y=-40.8935 Z=0
    g204: Circle CenterX=306.073 CenterY=73.3346 CenterZ=0 NormalX=0 NormalY=0 NormalZ=1 AngleXU=0 Radius=1
    g205: Circle CenterX=306.073 CenterY=77.3346 CenterZ=0 NormalX=0 NormalY=0 NormalZ=1 AngleXU=0 Radius=1
    g206: Circle CenterX=302.567 CenterY=75.4095 CenterZ=0 NormalX=0 NormalY=0 NormalZ=1 AngleXU=0 Radius=1
    g207: BSplineCurve PolesCount=3 KnotsCount=2 Degree=2 IsPeriodic=0
    g208: GeomPoint X=306.073 Y=73.3346 Z=0
    g209: GeomPoint X=302.567 Y=75.4095 Z=0
    g210: LineSegment StartX=302.567 StartY=-42.9683 StartZ=0 EndX=198.275 EndY=14.2954 EndZ=0
    g211: LineSegment StartX=198.275 StartY=18.1458 StartZ=0 EndX=302.567 EndY=75.4095 EndZ=0
    g212: LineSegment StartX=306.073 StartY=73.3346 StartZ=0 EndX=306.073 EndY=-40.8935 EndZ=0
    g213: LineSegment StartX=322.073 StartY=105.865 StartZ=0 EndX=328.643 EndY=105.865 EndZ=0
    g214: LineSegment StartX=318.073 StartY=120.221 StartZ=0 EndX=318.073 EndY=109.865 EndZ=0
    g215: LineSegment StartX=336.157 StartY=107.779 StartZ=0 EndX=362.567 EndY=122.294 EndZ=0
    g216: Circle CenterX=362.073 CenterY=124.221 CenterZ=0 NormalX=0 NormalY=0 NormalZ=1 AngleXU=0 Radius=1
    g217: Circle CenterX=366.073 CenterY=124.221 CenterZ=0 NormalX=0 NormalY=0 NormalZ=1 AngleXU=0 Radius=1
    g218: Circle CenterX=362.567 CenterY=122.294 CenterZ=0 NormalX=0 NormalY=0 NormalZ=1 AngleXU=0 Radius=1
    g219: BSplineCurve PolesCount=3 KnotsCount=2 Degree=2 IsPeriodic=0
    g220: GeomPoint X=362.073 Y=124.221 Z=0
    g221: GeomPoint X=362.567 Y=122.294 Z=0
    g222: Circle CenterX=322.073 CenterY=124.221 CenterZ=0 NormalX=0 NormalY=0 NormalZ=1 AngleXU=0 Radius=1
    g223: Circle CenterX=318.073 CenterY=124.221 CenterZ=0 NormalX=0 NormalY=0 NormalZ=1 AngleXU=0 Radius=1
    g224: Circle CenterX=318.073 CenterY=120.221 CenterZ=0 NormalX=0 NormalY=0 NormalZ=1 AngleXU=0 Radius=1
    g225: BSplineCurve PolesCount=3 KnotsCount=2 Degree=2 IsPeriodic=0
    g226: GeomPoint X=322.073 Y=124.221 Z=0
    g227: GeomPoint X=318.073 Y=120.221 Z=0
    g228: Circle CenterX=322.073 CenterY=105.865 CenterZ=0 NormalX=0 NormalY=0 NormalZ=1 AngleXU=0 Radius=1
    g229: Circle CenterX=318.073 CenterY=105.865 CenterZ=0 NormalX=0 NormalY=0 NormalZ=1 AngleXU=0 Radius=1
    g230: Circle CenterX=318.073 CenterY=109.865 CenterZ=0 NormalX=0 NormalY=0 NormalZ=1 AngleXU=0 Radius=1
    g231: BSplineCurve PolesCount=3 KnotsCount=2 Degree=2 IsPeriodic=0
    g232: GeomPoint X=322.073 Y=105.865 Z=0
    g233: GeomPoint X=318.073 Y=109.865 Z=0
    g234: Circle CenterX=336.157 CenterY=107.779 CenterZ=0 NormalX=0 NormalY=0 NormalZ=1 AngleXU=0 Radius=1
    g235: Circle CenterX=332.651 CenterY=105.853 CenterZ=0 NormalX=0 NormalY=0 NormalZ=1 AngleXU=0 Radius=1
    g236: Circle CenterX=328.643 CenterY=105.865 CenterZ=0 NormalX=0 NormalY=0 NormalZ=1 AngleXU=0 Radius=1
    g237: BSplineCurve PolesCount=3 KnotsCount=2 Degree=2 IsPeriodic=0
    g238: GeomPoint X=336.157 Y=107.779 Z=0
    g239: GeomPoint X=328.643 Y=105.865 Z=0
    g240: LineSegment StartX=322.073 StartY=124.221 StartZ=0 EndX=362.073 EndY=124.221 EndZ=0
    g241: Circle CenterX=371.567 CenterY=-80.8644 CenterZ=0 NormalX=0 NormalY=0 NormalZ=1 AngleXU=0 Radius=1
    g242: Circle CenterX=375.073 CenterY=-82.7896 CenterZ=0 NormalX=0 NormalY=0 NormalZ=1 AngleXU=0 Radius=1
    g243: Circle CenterX=375.073 CenterY=-78.7896 CenterZ=0 NormalX=0 NormalY=0 NormalZ=1 AngleXU=0 Radius=1
    g244: BSplineCurve PolesCount=3 KnotsCount=2 Degree=2 IsPeriodic=0
    g245: GeomPoint X=371.567 Y=-80.8644 Z=0
    g246: GeomPoint X=375.073 Y=-78.7896 Z=0
    g247: Circle CenterX=321.579 CenterY=-53.4075 CenterZ=0 NormalX=0 NormalY=0 NormalZ=1 AngleXU=0 Radius=1
    g248: Circle CenterX=318.073 CenterY=-51.4823 CenterZ=0 NormalX=0 NormalY=0 NormalZ=1 AngleXU=0 Radius=1
    g249: Circle CenterX=318.073 CenterY=-47.4805 CenterZ=0 NormalX=0 NormalY=0 NormalZ=1 AngleXU=0 Radius=1
    g250: BSplineCurve PolesCount=3 KnotsCount=2 Degree=2 IsPeriodic=0
    g251: GeomPoint X=321.579 Y=-53.4075 Z=0
    g252: GeomPoint X=318.073 Y=-47.4805 Z=0
    g253: LineSegment StartX=371.567 StartY=-80.8644 StartZ=0 EndX=321.579 EndY=-53.4075 EndZ=0
    g254: Circle CenterX=321.579 CenterY=-67.3492 CenterZ=0 NormalX=0 NormalY=0 NormalZ=1 AngleXU=0 Radius=1
    g255: Circle CenterX=318.073 CenterY=-65.424 CenterZ=0 NormalX=0 NormalY=0 NormalZ=1 AngleXU=0 Radius=1
    g256: Circle CenterX=318.073 CenterY=-69.424 CenterZ=0 NormalX=0 NormalY=0 NormalZ=1 AngleXU=0 Radius=1
    g257: BSplineCurve PolesCount=3 KnotsCount=2 Degree=2 IsPeriodic=0
    g258: GeomPoint X=321.579 Y=-67.3492 Z=0
    g259: GeomPoint X=318.073 Y=-69.424 Z=0
    g260: Circle CenterX=362.567 CenterY=-89.8542 CenterZ=0 NormalX=0 NormalY=0 NormalZ=1 AngleXU=0 Radius=1
    g261: Circle CenterX=366.073 CenterY=-91.7794 CenterZ=0 NormalX=0 NormalY=0 NormalZ=1 AngleXU=0 Radius=1
    g262: Circle CenterX=362.073 CenterY=-91.7794 CenterZ=0 NormalX=0 NormalY=0 NormalZ=1 AngleXU=0 Radius=1
    g263: BSplineCurve PolesCount=3 KnotsCount=2 Degree=2 IsPeriodic=0
    g264: GeomPoint X=362.567 Y=-89.8542 Z=0
    g265: GeomPoint X=362.073 Y=-91.7794 Z=0
    g266: Circle CenterX=322.073 CenterY=-91.7794 CenterZ=0 NormalX=0 NormalY=0 NormalZ=1 AngleXU=0 Radius=1
    g267: Circle CenterX=318.073 CenterY=-91.7794 CenterZ=0 NormalX=0 NormalY=0 NormalZ=1 AngleXU=0 Radius=1
    g268: Circle CenterX=318.073 CenterY=-87.7794 CenterZ=0 NormalX=0 NormalY=0 NormalZ=1 AngleXU=0 Radius=1
    g269: BSplineCurve PolesCount=3 KnotsCount=2 Degree=2 IsPeriodic=0
    g270: GeomPoint X=322.073 Y=-91.7794 Z=0
    g271: GeomPoint X=318.073 Y=-87.7794 Z=0
    g272: LineSegment StartX=362.567 StartY=-89.8542 StartZ=0 EndX=321.579 EndY=-67.3492 EndZ=0
    g273: LineSegment StartX=318.073 StartY=-69.424 StartZ=0 EndX=318.073 EndY=-87.7794 EndZ=0
    g274: LineSegment StartX=322.073 StartY=-91.7794 StartZ=0 EndX=362.073 EndY=-91.7794 EndZ=0
    g275: Circle CenterX=2.07281 CenterY=124.221 CenterZ=0 NormalX=0 NormalY=0 NormalZ=1 AngleXU=0 Radius=1
    g276: Circle CenterX=1.57905 CenterY=122.295 CenterZ=0 NormalX=0 NormalY=0 NormalZ=1 AngleXU=0 Radius=1
    g277: BSplineCurve PolesCount=3 KnotsCount=2 Degree=2 IsPeriodic=0
    g278: GeomPoint X=2.07281 Y=124.221 Z=0
    g279: GeomPoint X=1.57905 Y=122.295 Z=0
    g280: Circle CenterX=42.0728 CenterY=124.221 CenterZ=0 NormalX=0 NormalY=0 NormalZ=1 AngleXU=0 Radius=1
    g281: Circle CenterX=46.0728 CenterY=124.221 CenterZ=0 NormalX=0 NormalY=0 NormalZ=1 AngleXU=0 Radius=1
    g282: Circle CenterX=46.0728 CenterY=120.221 CenterZ=0 NormalX=0 NormalY=0 NormalZ=1 AngleXU=0 Radius=1
    g283: BSplineCurve PolesCount=3 KnotsCount=2 Degree=2 IsPeriodic=0
    g284: GeomPoint X=42.0728 Y=124.221 Z=0
    g285: GeomPoint X=46.0728 Y=120.221 Z=0
    g286: Circle CenterX=46.0728 CenterY=109.865 CenterZ=0 NormalX=0 NormalY=0 NormalZ=1 AngleXU=0 Radius=1
    g287: Circle CenterX=46.0728 CenterY=105.865 CenterZ=0 NormalX=0 NormalY=0 NormalZ=1 AngleXU=0 Radius=1
    g288: Circle CenterX=42.0728 CenterY=105.865 CenterZ=0 NormalX=0 NormalY=0 NormalZ=1 AngleXU=0 Radius=1
    g289: BSplineCurve PolesCount=3 KnotsCount=2 Degree=2 IsPeriodic=0
    g290: GeomPoint X=46.0728 Y=109.865 Z=0
    g291: GeomPoint X=42.0728 Y=105.865 Z=0
    g292: Circle CenterX=35.5028 CenterY=105.865 CenterZ=0 NormalX=0 NormalY=0 NormalZ=1 AngleXU=0 Radius=1
    g293: Circle CenterX=31.5028 CenterY=105.865 CenterZ=0 NormalX=0 NormalY=0 NormalZ=1 AngleXU=0 Radius=1
    g294: Circle CenterX=27.9965 CenterY=107.79 CenterZ=0 NormalX=0 NormalY=0 NormalZ=1 AngleXU=0 Radius=1
    g295: BSplineCurve PolesCount=3 KnotsCount=2 Degree=2 IsPeriodic=0
    g296: GeomPoint X=35.5028 Y=105.865 Z=0
    g297: GeomPoint X=27.9965 Y=107.79 Z=0
    g298: LineSegment StartX=2.07281 StartY=124.221 StartZ=0 EndX=42.0728 EndY=124.221 EndZ=0
    g299: LineSegment StartX=46.0728 StartY=120.221 StartZ=0 EndX=46.0728 EndY=109.865 EndZ=0
    g300: LineSegment StartX=42.0728 StartY=105.865 StartZ=0 EndX=35.5028 EndY=105.865 EndZ=0
    g301: LineSegment StartX=27.9965 StartY=107.79 StartZ=0 EndX=1.57905 EndY=122.295 EndZ=0
    g302: Circle CenterX=42.5666 CenterY=-67.3492 CenterZ=0 NormalX=0 NormalY=0 NormalZ=1 AngleXU=0 Radius=1
    g303: Circle CenterX=46.0728 CenterY=-65.424 CenterZ=0 NormalX=0 NormalY=0 NormalZ=1 AngleXU=0 Radius=1
    g304: Circle CenterX=46.0728 CenterY=-69.424 CenterZ=0 NormalX=0 NormalY=0 NormalZ=1 AngleXU=0 Radius=1
    g305: BSplineCurve PolesCount=3 KnotsCount=2 Degree=2 IsPeriodic=0
    g306: GeomPoint X=42.5666 Y=-67.3492 Z=0
    g307: GeomPoint X=46.0728 Y=-69.424 Z=0
    g308: Circle CenterX=46.0728 CenterY=-87.7794 CenterZ=0 NormalX=0 NormalY=0 NormalZ=1 AngleXU=0 Radius=1
    g309: Circle CenterX=46.0728 CenterY=-91.7794 CenterZ=0 NormalX=0 NormalY=0 NormalZ=1 AngleXU=0 Radius=1
    g310: Circle CenterX=42.0728 CenterY=-91.7794 CenterZ=0 NormalX=0 NormalY=0 NormalZ=1 AngleXU=0 Radius=1
    g311: BSplineCurve PolesCount=3 KnotsCount=2 Degree=2 IsPeriodic=0
    g312: GeomPoint X=46.0728 Y=-87.7794 Z=0
    g313: GeomPoint X=42.0728 Y=-91.7794 Z=0
    g314: Circle CenterX=2.07281 CenterY=-91.7794 CenterZ=0 NormalX=0 NormalY=0 NormalZ=1 AngleXU=0 Radius=1
    g315: Circle CenterX=-1.92719 CenterY=-91.7794 CenterZ=0 NormalX=0 NormalY=0 NormalZ=1 AngleXU=0 Radius=1
    g316: Circle CenterX=1.57905 CenterY=-89.8542 CenterZ=0 NormalX=0 NormalY=0 NormalZ=1 AngleXU=0 Radius=1
    g317: BSplineCurve PolesCount=3 KnotsCount=2 Degree=2 IsPeriodic=0
    g318: GeomPoint X=2.07281 Y=-91.7794 Z=0
    g319: GeomPoint X=1.57905 Y=-89.8542 Z=0
    g320: LineSegment StartX=2.07281 StartY=-91.7794 StartZ=0 EndX=42.0728 EndY=-91.7794 EndZ=0
    g321: LineSegment StartX=46.0728 StartY=-87.7794 StartZ=0 EndX=46.0728 EndY=-69.424 EndZ=0
    g322: LineSegment StartX=42.5666 StartY=-67.3492 StartZ=0 EndX=1.57905 EndY=-89.8542 EndZ=0
    g323: Circle CenterX=322.073 CenterY=76.4095 CenterZ=0 NormalX=0 NormalY=0 NormalZ=1 AngleXU=0 Radius=4
    g324: BSplineCurve PolesCount=3 KnotsCount=2 Degree=2 IsPeriodic=0
    g325: GeomPoint X=318.073 Y=72.4095 Z=0
    g326: GeomPoint X=322.073 Y=76.4095 Z=0
    g327: Circle CenterX=375.073 CenterY=72.4095 CenterZ=0 NormalX=0 NormalY=0 NormalZ=1 AngleXU=0 Radius=1
    g328: Circle CenterX=375.073 CenterY=76.4095 CenterZ=0 NormalX=0 NormalY=0 NormalZ=1 AngleXU=0 Radius=1
    g329: Circle CenterX=371.073 CenterY=76.4095 CenterZ=0 NormalX=0 NormalY=0 NormalZ=1 AngleXU=0 Radius=1
    g330: BSplineCurve PolesCount=3 KnotsCount=2 Degree=2 IsPeriodic=0
    g331: GeomPoint X=375.073 Y=72.4095 Z=0
    g332: GeomPoint X=371.073 Y=76.4095 Z=0
    g333: LineSegment StartX=322.073 StartY=76.4095 StartZ=0 EndX=371.073 EndY=76.4095 EndZ=0
    g334: LineSegment StartX=318.073 StartY=72.4095 StartZ=0 EndX=318.073 EndY=-47.4805 EndZ=0
    g335: LineSegment StartX=375.073 StartY=72.4095 StartZ=0 EndX=375.073 EndY=-78.7896 EndZ=0
    g336: ArcOfCircle CenterX=-26.9272 CenterY=22.1087 CenterZ=0 NormalX=0 NormalY=0 NormalZ=1 AngleXU=0 Radius=4 StartAngle=5e-16 EndAngle=3.14159
    g337: LineSegment StartX=-22.9272 StartY=22.1087 StartZ=0 EndX=-18.9272 EndY=-83.7794 EndZ=0
    g338: LineSegment StartX=-34.9272 StartY=-83.7794 StartZ=0 EndX=-30.9272 EndY=22.1087 EndZ=0
    g339: ArcOfCircle CenterX=391.073 CenterY=22.1087 CenterZ=0 NormalX=0 NormalY=0 NormalZ=1 AngleXU=0 Radius=4 StartAngle=0 EndAngle=3.14159
    g340: LineSegment StartX=387.073 StartY=22.1087 StartZ=0 EndX=383.073 EndY=-83.7794 EndZ=0
    g341: LineSegment StartX=395.073 StartY=22.1087 StartZ=0 EndX=399.073 EndY=-83.7794 EndZ=0
    g342: Circle CenterX=-10.9272 CenterY=-78.7794 CenterZ=0 NormalX=0 NormalY=0 NormalZ=1 AngleXU=0 Radius=1
    g343: Circle CenterX=-10.9272 CenterY=-82.7794 CenterZ=0 NormalX=0 NormalY=0 NormalZ=1 AngleXU=0 Radius=1
    g344: Circle CenterX=-7.42095 CenterY=-80.8542 CenterZ=0 NormalX=0 NormalY=0 NormalZ=1 AngleXU=0 Radius=1
    g345: BSplineCurve PolesCount=3 KnotsCount=2 Degree=2 IsPeriodic=0
    g346: GeomPoint X=-10.9272 Y=-78.7794 Z=0
    g347: GeomPoint X=-7.42095 Y=-80.8542 Z=0
    g348: Circle CenterX=42.5666 CenterY=-53.4075 CenterZ=0 NormalX=0 NormalY=0 NormalZ=1 AngleXU=0 Radius=1
    g349: Circle CenterX=46.0728 CenterY=-51.4823 CenterZ=0 NormalX=0 NormalY=0 NormalZ=1 AngleXU=0 Radius=1
    g350: Circle CenterX=46.0728 CenterY=-47.4823 CenterZ=0 NormalX=0 NormalY=0 NormalZ=1 AngleXU=0 Radius=1
    g351: BSplineCurve PolesCount=3 KnotsCount=2 Degree=2 IsPeriodic=0
    g352: GeomPoint X=42.5666 Y=-53.4075 Z=0
    g353: GeomPoint X=46.0728 Y=-47.4823 Z=0
    g354: Circle CenterX=46.0728 CenterY=72.4095 CenterZ=0 NormalX=0 NormalY=0 NormalZ=1 AngleXU=0 Radius=1
    g355: Circle CenterX=46.0728 CenterY=76.4095 CenterZ=0 NormalX=0 NormalY=0 NormalZ=1 AngleXU=0 Radius=1
    g356: Circle CenterX=42.0728 CenterY=76.4095 CenterZ=0 NormalX=0 NormalY=0 NormalZ=1 AngleXU=0 Radius=1
    g357: BSplineCurve PolesCount=3 KnotsCount=2 Degree=2 IsPeriodic=0
    g358: GeomPoint X=46.0728 Y=72.4095 Z=0
    g359: GeomPoint X=42.0728 Y=76.4095 Z=0
    g360: Circle CenterX=-6.92718 CenterY=76.4095 CenterZ=0 NormalX=0 NormalY=0 NormalZ=1 AngleXU=0 Radius=1
    g361: Circle CenterX=-10.9272 CenterY=76.4095 CenterZ=0 NormalX=0 NormalY=0 NormalZ=1 AngleXU=0 Radius=1
    g362: Circle CenterX=-10.9272 CenterY=72.4095 CenterZ=0 NormalX=0 NormalY=0 NormalZ=1 AngleXU=0 Radius=1
    g363: BSplineCurve PolesCount=3 KnotsCount=2 Degree=2 IsPeriodic=0
    g364: GeomPoint X=-6.92718 Y=76.4095 Z=0
    g365: GeomPoint X=-10.9272 Y=72.4095 Z=0
    g366: LineSegment StartX=-10.9272 StartY=72.4095 StartZ=0 EndX=-10.9272 EndY=-78.7794 EndZ=0
    g367: LineSegment StartX=-7.42095 StartY=-80.8542 StartZ=0 EndX=42.5666 EndY=-53.4075 EndZ=0
    g368: LineSegment StartX=46.0728 StartY=-47.4823 StartZ=0 EndX=46.0728 EndY=72.4095 EndZ=0
    g369: LineSegment StartX=42.0728 StartY=76.4095 StartZ=0 EndX=-6.92719 EndY=76.4095 EndZ=0
    g370: LineSegment StartX=232.072 StartY=136.221 StartZ=0 EndX=232.072 EndY=-117.815 EndZ=0
    g371: LineSegment StartX=245.072 StartY=136.221 StartZ=0 EndX=245.072 EndY=-116.499 EndZ=0
    g372: LineSegment StartX=119.072 StartY=136.221 StartZ=0 EndX=119.072 EndY=-116.228 EndZ=0
    g373: LineSegment StartX=-42.9272 StartY=136.221 StartZ=0 EndX=407.073 EndY=136.221 EndZ=0
    g374: LineSegment StartX=232.072 StartY=136.221 StartZ=0 EndX=220.072 EndY=136.221 EndZ=0
    g375: LineSegment StartX=232.072 StartY=136.221 StartZ=0 EndX=232.072 EndY=124.221 EndZ=0
    g376: LineSegment StartX=220.072 StartY=136.221 StartZ=0 EndX=220.072 EndY=124.221 EndZ=0
    g377: LineSegment StartX=220.072 StartY=136.221 StartZ=0 EndX=226.072 EndY=136.221 EndZ=0
    g378: LineSegment StartX=220.072 StartY=136.221 StartZ=0 EndX=220.072 EndY=130.221 EndZ=0
    g379: LineSegment StartX=220.072 StartY=124.221 StartZ=0 EndX=226.072 EndY=124.221 EndZ=0
    g380: LineSegment StartX=232.072 StartY=124.221 StartZ=0 EndX=232.072 EndY=127.221 EndZ=0
    g381: LineSegment StartX=232.072 StartY=136.221 StartZ=0 EndX=232.072 EndY=133.221 EndZ=0
    g382-g386: Circle x5 (B-spline internal-alignment scaffolding for g387; pole/knot coordinates omitted)
    g387: BSplineCurve PolesCount=5 KnotsCount=3 Degree=3 IsPeriodic=0
    g388: GeomPoint X=232.072 Y=133.221 Z=0
    g389: GeomPoint X=223.072 Y=130.221 Z=0
    g390: GeomPoint X=232.072 Y=127.221 Z=0
    g391: LineSegment StartX=189.124 StartY=124.221 StartZ=0 EndX=302.073 EndY=124.221 EndZ=0
    g392: LineSegment StartX=132.072 StartY=136.221 StartZ=0 EndX=132.072 EndY=124.221 EndZ=0
    g393: LineSegment StartX=132.072 StartY=136.221 StartZ=0 EndX=144.072 EndY=136.221 EndZ=0
    g394: LineSegment StartX=144.072 StartY=136.221 StartZ=0 EndX=144.072 EndY=124.221 EndZ=0
    g395: LineSegment StartX=144.072 StartY=136.221 StartZ=0 EndX=138.072 EndY=136.221 EndZ=0
    g396: LineSegment StartX=144.072 StartY=136.221 StartZ=0 EndX=144.072 EndY=130.221 EndZ=0
    g397: LineSegment StartX=132.072 StartY=136.221 StartZ=0 EndX=132.072 EndY=133.221 EndZ=0
    g398: LineSegment StartX=132.072 StartY=133.221 StartZ=0 EndX=132.072 EndY=127.221 EndZ=0
    g399-g403: Circle x5 (B-spline internal-alignment scaffolding for g404; pole/knot coordinates omitted)
    g404: BSplineCurve PolesCount=5 KnotsCount=3 Degree=3 IsPeriodic=0
    g405: GeomPoint X=132.072 Y=133.221 Z=0
    g406: GeomPoint X=141.072 Y=130.221 Z=0
    g407: GeomPoint X=132.072 Y=127.221 Z=0
    ... +8 more geometry lines
  constraints (706):
    c: Vertical(g0)
    c: Vertical(g1)
    c: Block(g1)
    c: Block(g0)
    c: Weight(g4) = 1
    c: Equal(g4,g5)
    c: Equal(g4,g6)
    c: InternalAlignment(g4,g7)
    c: InternalAlignment(g5,g7)
    c: InternalAlignment(g6,g7)
    c: InternalAlignment(g8,g7)
    c: InternalAlignment(g9,g7)
    c: Weight(g10) = 1
    c: Equal(g10,g11)
    c: Equal(g10,g12)
    c: InternalAlignment(g10,g13)
    c: InternalAlignment(g11,g13)
    c: InternalAlignment(g12,g13)
    c: InternalAlignment(g14,g13)
    c: InternalAlignment(g15,g13)
    c: Block(g13)
    c: Block(g7)
    c: Weight(g16) = 1
    c: Equal(g16,g17)
    c: Equal(g16,g18)
    c: InternalAlignment(g16,g19)
    c: InternalAlignment(g17,g19)
    c: InternalAlignment(g18,g19)
    c: InternalAlignment(g20,g19)
    c: InternalAlignment(g21,g19)
    c: Weight(g22) = 1
    c: Equal(g22,g23)
    c: Equal(g22,g24)
    c: InternalAlignment(g22,g25)
    c: InternalAlignment(g23,g25)
    c: InternalAlignment(g24,g25)
    c: InternalAlignment(g26,g25)
    c: InternalAlignment(g27,g25)
    c: Block(g25)
    c: Block(g19)
    c: Weight(g28) = 1
    c: Equal(g28,g29)
    c: Equal(g28,g30)
    c: InternalAlignment(g28,g31)
    c: InternalAlignment(g29,g31)
    c: InternalAlignment(g30,g31)
    c: InternalAlignment(g32,g31)
    c: InternalAlignment(g33,g31)
    c: Weight(g34) = 1
    c: Equal(g34,g35)
    c: Equal(g34,g36)
    c: InternalAlignment(g34,g37)
    c: InternalAlignment(g35,g37)
    c: InternalAlignment(g36,g37)
    c: InternalAlignment(g38,g37)
    c: InternalAlignment(g39,g37)
    c: Block(g31)
    c: Block(g37)
    c: Coincident(g40,g1)
    c: Coincident(g40,g0)
    c: Horizontal(g40)
    c: Distance(g40) = 450
    c: Weight(g41) = 1
    c: Equal(g41,g42)
    c: Equal(g41,g43)
    c: InternalAlignment(g41,g44)
    c: InternalAlignment(g42,g44)
    c: InternalAlignment(g43,g44)
    c: InternalAlignment(g45,g44)
    c: InternalAlignment(g46,g44)
    c: Block(g44)
    c: Weight(g47) = 1
    c: Equal(g47,g48)
    c: Equal(g47,g49)
    c: InternalAlignment(g47,g50)
    c: InternalAlignment(g48,g50)
    c: InternalAlignment(g49,g50)
    c: InternalAlignment(g51,g50)
    c: InternalAlignment(g52,g50)
    c: Block(g50)
    c: Weight(g53) = 1
    c: Equal(g53,g54)
    c: Equal(g53,g55)
    c: InternalAlignment(g53,g56)
    c: InternalAlignment(g54,g56)
    c: InternalAlignment(g55,g56)
    c: InternalAlignment(g57,g56)
    c: InternalAlignment(g58,g56)
    c: Block(g56)
    c: Weight(g59) = 1
    c: Equal(g59,g60)
    c: Equal(g59,g61)
    c: InternalAlignment(g59,g62)
    c: InternalAlignment(g60,g62)
    c: InternalAlignment(g61,g62)
    c: InternalAlignment(g63,g62)
    c: InternalAlignment(g64,g62)
    c: Block(g62)
    c: Weight(g65) = 1
    c: Equal(g65,g66)
    c: Equal(g65,g67)
    c: InternalAlignment(g65,g68)
    c: InternalAlignment(g66,g68)
    c: InternalAlignment(g67,g68)
    c: InternalAlignment(g69,g68)
    c: InternalAlignment(g70,g68)
    c: Weight(g71) = 1
    c: Equal(g71,g72)
    c: Equal(g71,g73)
    c: InternalAlignment(g71,g74)
    c: InternalAlignment(g72,g74)
    c: InternalAlignment(g73,g74)
    c: InternalAlignment(g75,g74)
    c: InternalAlignment(g76,g74)
    c: Block(g68)
    c: Block(g74)
    c: Coincident(g77,g68)
    c: Coincident(g77,g74)
    c: Vertical(g77)
    c: Coincident(g78,g68)
    c: Coincident(g78,g50)
    c: Coincident(g79,g50)
    c: Coincident(g79,g74)
    c: Weight(g80) = 1
    c: Equal(g80,g81)
    c: Equal(g80,g82)
    c: InternalAlignment(g80,g83)
    c: InternalAlignment(g81,g83)
    c: InternalAlignment(g82,g83)
    c: InternalAlignment(g84,g83)
    c: InternalAlignment(g85,g83)
    c: Weight(g86) = 1
    c: Equal(g86,g87)
    c: Equal(g86,g88)
    c: InternalAlignment(g86,g89)
    c: InternalAlignment(g87,g89)
    c: InternalAlignment(g88,g89)
    c: InternalAlignment(g90,g89)
    c: InternalAlignment(g91,g89)
    c: Block(g83)
    c: Block(g89)
    c: Coincident(g92,g83)
    c: Coincident(g92,g89)
    c: Vertical(g92)
    c: Coincident(g93,g83)
    c: Coincident(g93,g44)
    c: Coincident(g94,g44)
    c: Coincident(g94,g89)
    c: Weight(g95) = 1
    c: Equal(g95,g96)
    c: Equal(g95,g97)
    c: InternalAlignment(g95,g98)
    c: InternalAlignment(g96,g98)
    c: InternalAlignment(g97,g98)
    c: InternalAlignment(g99,g98)
    c: InternalAlignment(g100,g98)
    c: Weight(g101) = 1
    c: Equal(g101,g102)
    c: Equal(g101,g103)
    c: InternalAlignment(g101,g104)
    c: InternalAlignment(g102,g104)
    c: InternalAlignment(g103,g104)
    c: InternalAlignment(g105,g104)
    c: InternalAlignment(g106,g104)
    c: Block(g98)
    c: Block(g104)
    c: Coincident(g107,g98)
    c: Coincident(g107,g104)
    c: Vertical(g107)
    c: Coincident(g108,g104)
    c: Coincident(g108,g62)
    c: Coincident(g109,g62)
    c: Coincident(g109,g98)
    c: Weight(g110) = 1
    c: Equal(g110,g111)
    c: Equal(g110,g112)
    c: InternalAlignment(g110,g113)
    c: InternalAlignment(g111,g113)
    c: InternalAlignment(g112,g113)
    c: InternalAlignment(g114,g113)
    c: InternalAlignment(g115,g113)
    c: Weight(g116) = 1
    c: Equal(g116,g117)
    c: Equal(g116,g118)
    c: InternalAlignment(g116,g119)
    c: InternalAlignment(g117,g119)
    c: InternalAlignment(g118,g119)
    c: InternalAlignment(g120,g119)
    c: InternalAlignment(g121,g119)
    c: Block(g113)
    c: Block(g119)
    c: Coincident(g122,g113)
    c: Coincident(g122,g119)
    c: Vertical(g122)
    c: Coincident(g123,g119)
    c: Coincident(g123,g56)
    c: Coincident(g124,g56)
    c: Coincident(g124,g113)
    c: Weight(g125) = 1
    c: Equal(g125,g126)
    c: Equal(g125,g127)
    c: InternalAlignment(g125,g128)
    c: InternalAlignment(g126,g128)
    c: InternalAlignment(g127,g128)
    c: InternalAlignment(g129,g128)
    c: InternalAlignment(g130,g128)
    c: Weight(g131) = 1
    c: Equal(g131,g132)
    c: Equal(g131,g133)
    c: InternalAlignment(g131,g134)
    c: InternalAlignment(g132,g134)
    c: InternalAlignment(g133,g134)
    c: InternalAlignment(g135,g134)
    c: InternalAlignment(g136,g134)
    c: Weight(g137) = 1
    c: Equal(g137,g138)
    c: Equal(g137,g139)
    c: InternalAlignment(g137,g140)
    c: InternalAlignment(g138,g140)
    c: InternalAlignment(g139,g140)
    c: InternalAlignment(g141,g140)
    c: InternalAlignment(g142,g140)
    c: Weight(g143) = 1
    c: Equal(g143,g144)
    c: Equal(g143,g145)
    c: InternalAlignment(g143,g146)
    c: InternalAlignment(g144,g146)
    c: InternalAlignment(g145,g146)
    c: InternalAlignment(g147,g146)
    c: InternalAlignment(g148,g146)
    c: Block(g146)
    c: Block(g140)
    c: Block(g134)
    c: Block(g128)
    c: Coincident(g149,g25)
    c: Coincident(g149,g146)
    c: Coincident(g150,g146)
    c: Coincident(g150,g140)
    c: Horizontal(g150)
    c: Coincident(g151,g140)
    c: Coincident(g151,g25)
    c: Vertical(g151)
    c: Coincident(g152,g19)
    c: Coincident(g152,g134)
    c: Vertical(g152)
    c: Coincident(g153,g134)
    c: Coincident(g153,g128)
    c: Horizontal(g153)
    c: Coincident(g154,g128)
    c: Coincident(g154,g19)
    c: Weight(g155) = 1
    c: Equal(g155,g156)
    c: Equal(g155,g157)
    c: InternalAlignment(g155,g158)
    c: InternalAlignment(g156,g158)
    c: InternalAlignment(g157,g158)
    c: InternalAlignment(g159,g158)
    c: InternalAlignment(g160,g158)
    c: Weight(g161) = 1
    c: Equal(g161,g162)
    c: Equal(g161,g163)
    c: InternalAlignment(g161,g164)
    c: InternalAlignment(g162,g164)
    c: InternalAlignment(g163,g164)
    c: InternalAlignment(g165,g164)
    c: InternalAlignment(g166,g164)
    c: Weight(g167) = 1
    c: Equal(g167,g168)
    c: Equal(g167,g169)
    c: InternalAlignment(g167,g170)
    c: InternalAlignment(g168,g170)
    c: InternalAlignment(g169,g170)
    c: InternalAlignment(g171,g170)
    c: InternalAlignment(g172,g170)
    c: Weight(g173) = 1
    c: Equal(g173,g174)
    c: Equal(g173,g175)
    c: InternalAlignment(g173,g176)
    c: InternalAlignment(g174,g176)
    c: InternalAlignment(g175,g176)
    c: InternalAlignment(g177,g176)
    c: InternalAlignment(g178,g176)
    c: Block(g176)
    c: Block(g170)
    c: Block(g164)
    c: Block(g158)
    c: Coincident(g179,g170)
    c: Coincident(g179,g7)
    c: Vertical(g179)
    c: Coincident(g180,g13)
    c: Coincident(g180,g164)
    c: Vertical(g180)
    c: Coincident(g181,g158)
    c: Coincident(g181,g13)
    c: Coincident(g182,g7)
    c: Weight(g183) = 1
    c: Equal(g183,g184)
    c: Equal(g183,g185)
    c: InternalAlignment(g183,g186)
    c: InternalAlignment(g184,g186)
    c: InternalAlignment(g185,g186)
    c: InternalAlignment(g187,g186)
    c: InternalAlignment(g188,g186)
    c: Weight(g189) = 1
    c: Equal(g189,g190)
    c: Equal(g189,g191)
    c: InternalAlignment(g189,g192)
    c: InternalAlignment(g190,g192)
    c: InternalAlignment(g191,g192)
    c: InternalAlignment(g193,g192)
    c: InternalAlignment(g194,g192)
    c: Block(g192)
    c: Block(g186)
    c: Coincident(g195,g192)
    c: Coincident(g195,g31)
    c: Coincident(g196,g31)
    c: Coincident(g196,g186)
    c: Coincident(g197,g186)
    c: Coincident(g197,g192)
    c: Vertical(g197)
    c: Weight(g198) = 1
    c: Equal(g198,g199)
    c: Equal(g198,g200)
    c: InternalAlignment(g198,g201)
    c: InternalAlignment(g199,g201)
    c: InternalAlignment(g200,g201)
    c: InternalAlignment(g202,g201)
    c: InternalAlignment(g203,g201)
    c: Weight(g204) = 1
    c: Equal(g204,g205)
    c: Equal(g204,g206)
    c: InternalAlignment(g204,g207)
    c: InternalAlignment(g205,g207)
    c: InternalAlignment(g206,g207)
    c: InternalAlignment(g208,g207)
    c: InternalAlignment(g209,g207)
    c: Block(g207)
    c: Block(g201)
    c: Coincident(g210,g201)
    c: Coincident(g210,g37)
    c: Coincident(g211,g37)
    c: Coincident(g211,g207)
    c: Coincident(g212,g207)
    c: Coincident(g212,g201)
    c: Vertical(g212)
    c: Horizontal(g213)
    c: Block(g213)
    c: Vertical(g214)
    c: Block(g214)
    c: Block(g215)
    c: Weight(g216) = 1
    c: Equal(g216,g217)
    c: Equal(g216,g218)
    c: InternalAlignment(g216,g219)
    c: InternalAlignment(g217,g219)
    c: InternalAlignment(g218,g219)
    c: InternalAlignment(g220,g219)
    c: InternalAlignment(g221,g219)
    c: Weight(g222) = 1
    c: Equal(g222,g223)
    c: Equal(g222,g224)
    c: InternalAlignment(g222,g225)
    c: InternalAlignment(g223,g225)
    c: InternalAlignment(g224,g225)
    c: InternalAlignment(g226,g225)
    c: InternalAlignment(g227,g225)
    c: Weight(g228) = 1
    c: Equal(g228,g229)
    c: Equal(g228,g230)
    c: InternalAlignment(g228,g231)
    c: InternalAlignment(g229,g231)
    c: InternalAlignment(g230,g231)
    c: InternalAlignment(g232,g231)
    c: InternalAlignment(g233,g231)
    c: Weight(g234) = 1
    c: Equal(g234,g235)
    c: Equal(g234,g236)
    c: InternalAlignment(g234,g237)
    c: InternalAlignment(g235,g237)
    c: InternalAlignment(g236,g237)
    c: InternalAlignment(g238,g237)
    c: InternalAlignment(g239,g237)
    c: Block(g219)
    c: Block(g225)
    c: Block(g231)
    c: Block(g237)
    c: Coincident(g240,g225)
    c: Coincident(g240,g219)
    c: Horizontal(g240)
    c: Block(g182)
    c: Weight(g241) = 1
    c: Equal(g241,g242)
    c: Equal(g241,g243)
    c: InternalAlignment(g241,g244)
    c: InternalAlignment(g242,g244)
    c: InternalAlignment(g243,g244)
    c: InternalAlignment(g245,g244)
    c: InternalAlignment(g246,g244)
    c: Weight(g247) = 1
    c: Equal(g247,g248)
    c: Equal(g247,g249)
    c: InternalAlignment(g247,g250)
    c: InternalAlignment(g248,g250)
    c: InternalAlignment(g249,g250)
    c: InternalAlignment(g251,g250)
    c: InternalAlignment(g252,g250)
    c: Block(g244)
    c: Block(g250)
    c: Coincident(g253,g244)
    c: Coincident(g253,g250)
    c: Weight(g254) = 1
    c: Equal(g254,g255)
    c: Equal(g254,g256)
    c: InternalAlignment(g254,g257)
    c: InternalAlignment(g255,g257)
    c: InternalAlignment(g256,g257)
    c: InternalAlignment(g258,g257)
    c: InternalAlignment(g259,g257)
    c: Weight(g260) = 1
    c: Equal(g260,g261)
    c: Equal(g260,g262)
    c: InternalAlignment(g260,g263)
    c: InternalAlignment(g261,g263)
    c: InternalAlignment(g262,g263)
    c: InternalAlignment(g264,g263)
    c: InternalAlignment(g265,g263)
    c: Weight(g266) = 1
    c: Equal(g266,g267)
    c: Equal(g266,g268)
    c: InternalAlignment(g266,g269)
    c: InternalAlignment(g267,g269)
    c: InternalAlignment(g268,g269)
    c: InternalAlignment(g270,g269)
    c: InternalAlignment(g271,g269)
    c: Block(g269)
    c: Block(g263)
    c: Block(g257)
    c: Coincident(g272,g263)
    c: Coincident(g272,g257)
    c: Coincident(g273,g257)
    c: Coincident(g273,g269)
    c: Vertical(g273)
    c: Coincident(g274,g269)
    c: Coincident(g274,g263)
    c: Horizontal(g274)
    c: Weight(g275) = 1
    c: Equal(g275,g276)
    c: InternalAlignment(g275,g277)
    c: InternalAlignment(g276,g277)
    c: InternalAlignment(g278,g277)
    c: InternalAlignment(g279,g277)
    c: Weight(g280) = 1
    c: InternalAlignment(g281,g283)
    c: InternalAlignment(g282,g283)
    c: InternalAlignment(g284,g283)
    c: InternalAlignment(g285,g283)
    c: Weight(g286) = 1
    c: Equal(g286,g287)
    c: Equal(g286,g288)
    c: InternalAlignment(g286,g289)
    c: InternalAlignment(g287,g289)
    c: InternalAlignment(g288,g289)
    c: InternalAlignment(g290,g289)
    c: InternalAlignment(g291,g289)
    c: Equal(g292,g293)
    c: Equal(g292,g294)
    c: InternalAlignment(g292,g295)
    c: InternalAlignment(g293,g295)
    c: InternalAlignment(g294,g295)
    c: InternalAlignment(g296,g295)
    c: InternalAlignment(g297,g295)
    c: Block(g283)
    c: Block(g289)
    c: Block(g295)
    c: Block(g277)
    c: Coincident(g298,g277)
    c: Coincident(g298,g283)
    c: Horizontal(g298)
    c: Coincident(g299,g283)
    c: Coincident(g299,g289)
    c: Vertical(g299)
    c: Coincident(g300,g289)
    c: Coincident(g300,g295)
    c: Horizontal(g300)
    c: Coincident(g301,g295)
    c: Coincident(g301,g277)
    c: Weight(g302) = 1
    c: Equal(g302,g303)
    c: Equal(g302,g304)
    c: InternalAlignment(g302,g305)
    c: InternalAlignment(g303,g305)
    c: InternalAlignment(g304,g305)
    c: InternalAlignment(g306,g305)
    c: InternalAlignment(g307,g305)
    c: Weight(g308) = 1
    c: Equal(g308,g309)
    c: Equal(g308,g310)
    c: InternalAlignment(g308,g311)
    c: InternalAlignment(g309,g311)
    c: InternalAlignment(g310,g311)
    c: InternalAlignment(g312,g311)
    c: Weight(g314) = 1
    c: Equal(g314,g315)
    c: Equal(g314,g316)
    c: InternalAlignment(g314,g317)
    c: InternalAlignment(g315,g317)
    c: InternalAlignment(g316,g317)
    c: InternalAlignment(g318,g317)
    c: InternalAlignment(g319,g317)
    c: Block(g317)
    c: Block(g311)
    c: Block(g305)
    c: Coincident(g320,g317)
    c: Coincident(g320,g311)
    c: Horizontal(g320)
    c: Coincident(g321,g311)
    c: Coincident(g321,g305)
    c: Vertical(g321)
    c: Coincident(g322,g305)
    c: Coincident(g322,g317)
    c: InternalAlignment(g323,g324)
    c: InternalAlignment(g325,g324)
    c: InternalAlignment(g326,g324)
    c: Block(g324)
    c: Equal(g327,g328)
    c: Equal(g327,g329)
    c: InternalAlignment(g327,g330)
    c: InternalAlignment(g328,g330)
    c: InternalAlignment(g329,g330)
    c: InternalAlignment(g331,g330)
    c: InternalAlignment(g332,g330)
    c: Block(g330)
    c: Coincident(g333,g324)
    c: Horizontal(g333)
    c: Block(g333)
    c: Coincident(g334,g324)
    c: Coincident(g334,g250)
    c: Vertical(g334)
    c: Coincident(g335,g330)
    c: Coincident(g335,g244)
    c: Vertical(g335)
    c: Block(g336)
    c: Block(g2)
    c: Distance(g334) = 119.89
    c: Coincident(g337,g336)
    c: Coincident(g337,g2)
    c: Coincident(g338,g2)
    c: Coincident(g338,g336)
    c: Block(g3)
    c: Block(g339)
    c: Coincident(g340,g339)
    c: Coincident(g340,g3)
    c: Coincident(g341,g339)
    c: Coincident(g341,g3)
    c: Block(g341)
    c: Block(g340)
    c: Weight(g342) = 1
    c: Equal(g342,g343)
    c: Equal(g342,g344)
    c: InternalAlignment(g342,g345)
    c: InternalAlignment(g343,g345)
    c: InternalAlignment(g344,g345)
    c: InternalAlignment(g346,g345)
    c: InternalAlignment(g347,g345)
    c: Weight(g348) = 1
    c: Equal(g348,g349)
    c: Equal(g348,g350)
    c: InternalAlignment(g348,g351)
    c: InternalAlignment(g349,g351)
    c: InternalAlignment(g350,g351)
    c: InternalAlignment(g352,g351)
    c: InternalAlignment(g353,g351)
    c: Weight(g354) = 1
    c: Equal(g354,g355)
    c: Equal(g354,g356)
    c: InternalAlignment(g354,g357)
    c: InternalAlignment(g355,g357)
    c: InternalAlignment(g356,g357)
    c: InternalAlignment(g358,g357)
    c: InternalAlignment(g359,g357)
    c: Weight(g360) = 1
    c: Equal(g360,g361)
    c: Equal(g360,g362)
    c: InternalAlignment(g360,g363)
    c: InternalAlignment(g361,g363)
    c: InternalAlignment(g362,g363)
    c: InternalAlignment(g364,g363)
    c: InternalAlignment(g365,g363)
    c: Block(g363)
    c: Block(g357)
    c: Block(g351)
    c: Block(g345)
    c: Coincident(g366,g363)
    c: Coincident(g366,g345)
    c: Vertical(g366)
    c: Coincident(g367,g345)
    c: Coincident(g367,g351)
    c: Coincident(g368,g351)
    c: Coincident(g368,g357)
    c: Vertical(g368)
    c: Coincident(g369,g357)
    c: Coincident(g369,g363)
    c: Horizontal(g369)
    c: Vertical(g370)
    c: Vertical(g371)
    c: Vertical(g372)
    c: Coincident(g373,g0)
    c: Coincident(g373,g1)
    c: Horizontal(g373)
    c: Block(g373)
    c: Distance(g373) = 450
    c: Block(g371)
    c: Block(g370)
    c: Block(g372)
    c: Distance(g0) = 240
    c: Horizontal(g374)
    c: Distance(g374) = 12
    c: Coincident(g374,g370)
    c: Vertical(g375)
    c: Distance(g375) = 12
    c: Coincident(g375,g370)
    c: Coincident(g376,g374)
    c: Vertical(g376)
    c: Horizontal(g377)
    c: Vertical(g378)
    c: Distance(g378) = 6
    c: Coincident(g378,g374)
    c: Coincident(g377,g374)
    c: Block(g376)
    c: Coincident(g379,g376)
    c: Horizontal(g379)
    c: Distance(g379) = 6
    c: Vertical(g380)
    c: Distance(g380) = 3
    c: Vertical(g381)
    c: Distance(g381) = 3
    c: Coincident(g381,g370)
    c: Coincident(g375,g380)
    c: Coincident(g387,g381)
    c: Weight(g382) = 1
    c: Equal(g382,g383)
    c: Coincident(g383,g377)
    c: Equal(g382,g384)
    c: Coincident(g384,g378)
    c: Equal(g382,g385)
    c: Coincident(g385,g379)
    c: Equal(g382,g386)
    c: Coincident(g387,g380)
    c: InternalAlignment(g382-g386 -> g387) x5
    c: InternalAlignment(g388,g387)
    c: InternalAlignment(g389,g387)
    c: InternalAlignment(g390,g387)
    c: Coincident(g391,g164)
    c: Coincident(g391,g158)
    c: Horizontal(g391)
    c: Block(g387)
    c: Vertical(g392)
    c: Distance(g392) = 12
    c: Horizontal(g393)
    c: Distance(g393) = 12
    c: Coincident(g394,g393)
    c: Vertical(g394)
    c: Distance(g394) = 12
    c: Horizontal(g395)
    c: Distance(g395) = 6
    c: Coincident(g395,g393)
    c: Vertical(g396)
    c: Distance(g396) = 6
    c: Coincident(g396,g393)
    c: Vertical(g397)
    c: Distance(g397) = 3
    c: Vertical(g398)
    c: Distance(g398) = 6
    c: Coincident(g398,g397)
    c: Coincident(g404,g397)
    c: Weight(g399) = 1
    c: Equal(g399,g400)
    c: Coincident(g400,g395)
    c: Equal(g399,g401)
    c: Coincident(g401,g396)
    c: Equal(g399,g402)
    c: Equal(g399,g403)
    c: Coincident(g404,g398)
    c: InternalAlignment(g399-g403 -> g404) x5
    c: InternalAlignment(g405,g404)
    c: InternalAlignment(g406,g404)
    c: InternalAlignment(g407,g404)
    c: Coincident(g408,g392)
    c: Coincident(g408,g170)
    c: Horizontal(g408)
    c: Block(g404)
    c: Coincident(g409,g176)
    c: Coincident(g409,g392)
    c: Horizontal(g409)
    c: Block(g408)
    c: Coincident(g411,g392)
    c: PointOnObject(g411,g153)
    c: Vertical(g411)
    c: Vertical(g413)
    c: Equal(g394,g413) = 12
    c: Block(g412)
    c: Coincident(g414,g411)
    c: Coincident(g415,g412)
    c: Vertical(g415)
    c: PointOnObject(g415,g40)
    c: Block(g415)
FEATURE [Part::Extrusion] Extrude005
  Base = -> Sketch003
  Dir = (0,0,1)
  DirMode = 2
  FaceMakerClass = Part::FaceMakerBullseye
  LengthFwd = 24
  LengthRev = 0
  Solid = true
  Symmetric = false
